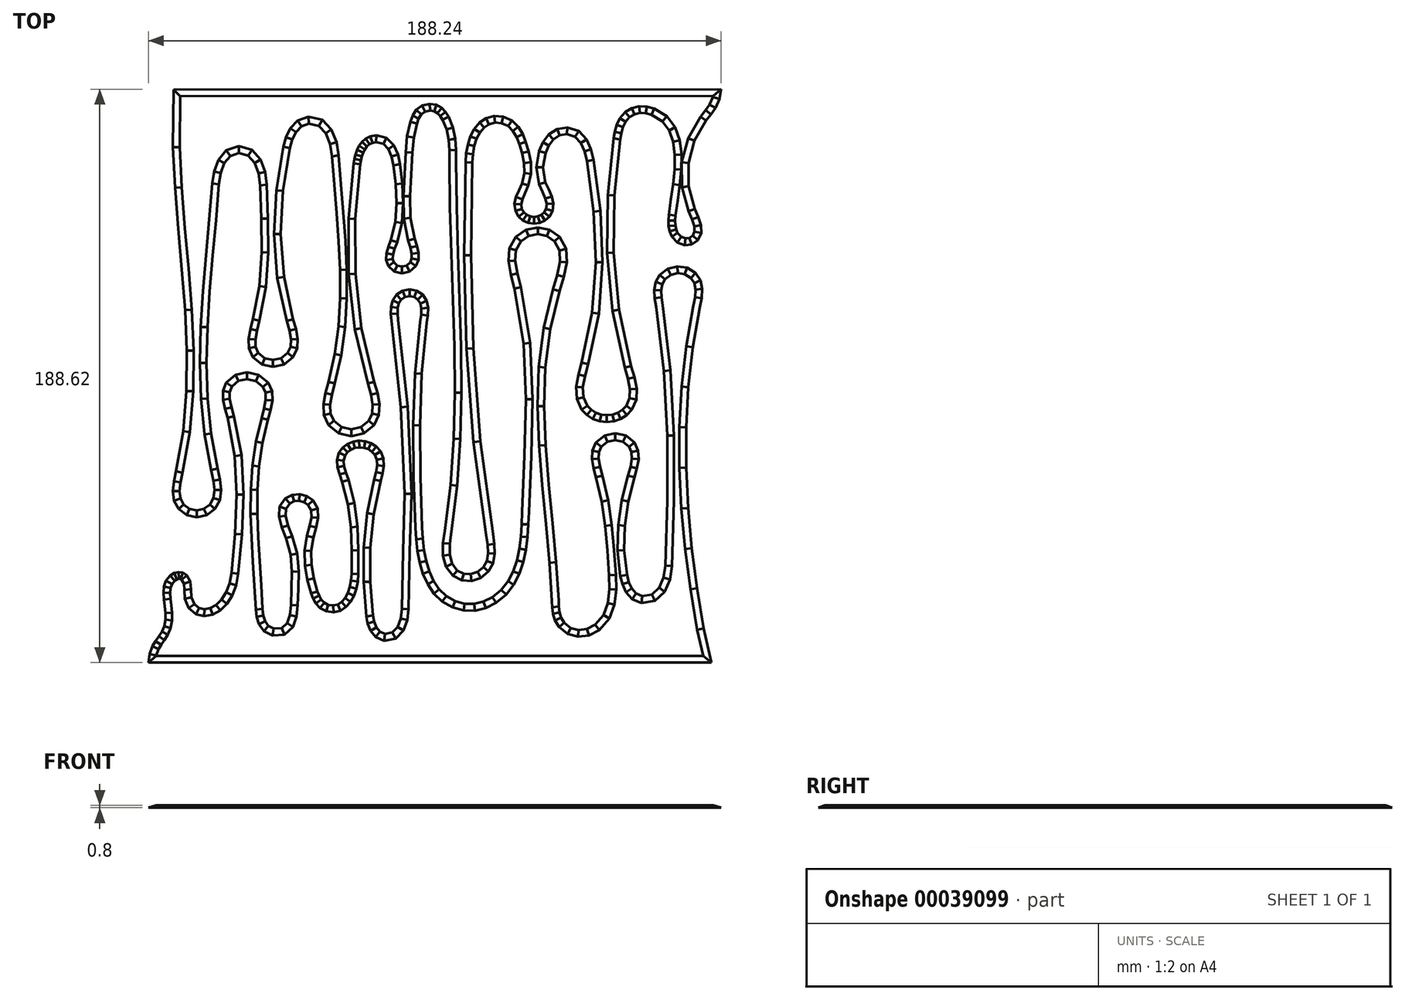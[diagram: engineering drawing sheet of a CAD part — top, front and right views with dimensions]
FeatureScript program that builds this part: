
annotation { "Feature Type Name" : "Feature", "Feature Type Description" : "" }
export const myFeature = defineFeature(function(context is Context, id is Id, definition is map)
    precondition{}
    {
        {
            var Q0;
            Q0=qCreatedBy(makeId("Top.planeOp"),FACE);
            var sketch = newSketch(context, id + "F0", { "sketchPlane" : qUnion([Q0])});
            skPoint(sketch, "E0.rect.middle", {"position": v(0, 0) * mm});
            skLineSegment(sketch, "E1", {"start": v(-85.88, 94.16) * mm, "end": v(-86.03, 75.24) * mm});
            skLineSegment(sketch, "E2", {"start": v(-86.03, 75.24) * mm, "end": v(-85.37, 61.84) * mm});
            skLineSegment(sketch, "E3", {"start": v(-85.37, 61.84) * mm, "end": v(-84.3, 48.43) * mm});
            skLineSegment(sketch, "E4", {"start": v(-84.3, 48.43) * mm, "end": v(-83.12, 35.03) * mm});
            skLineSegment(sketch, "E5", {"start": v(-83.12, 35.03) * mm, "end": v(-82.08, 21.66) * mm});
            skLineSegment(sketch, "E6", {"start": v(-82.08, 21.66) * mm, "end": v(-81.49, 8.31) * mm});
            skLineSegment(sketch, "E7", {"start": v(-81.49, 8.31) * mm, "end": v(-81.6, -4.99) * mm});
            skLineSegment(sketch, "E8", {"start": v(-81.6, -4.99) * mm, "end": v(-82.7, -18.23) * mm});
            skLineSegment(sketch, "E9", {"start": v(-82.7, -18.23) * mm, "end": v(-85.06, -31.41) * mm});
            skLineSegment(sketch, "E10", {"start": v(-85.06, -31.41) * mm, "end": v(-85.77, -34.7) * mm});
            skLineSegment(sketch, "E11", {"start": v(-85.77, -34.7) * mm, "end": v(-86.1, -37.97) * mm});
            skLineSegment(sketch, "E12", {"start": v(-86.1, -37.97) * mm, "end": v(-85.72, -41.07) * mm});
            skLineSegment(sketch, "E13", {"start": v(-85.72, -41.07) * mm, "end": v(-84.23, -43.82) * mm});
            skLineSegment(sketch, "E14", {"start": v(-84.23, -43.82) * mm, "end": v(-81.5, -45.83) * mm});
            skLineSegment(sketch, "E15", {"start": v(-81.5, -45.83) * mm, "end": v(-78.24, -46.5) * mm});
            skLineSegment(sketch, "E16", {"start": v(-78.24, -46.5) * mm, "end": v(-74.97, -45.83) * mm});
            skLineSegment(sketch, "E17", {"start": v(-74.97, -45.83) * mm, "end": v(-72.2, -43.82) * mm});
            skLineSegment(sketch, "E18", {"start": v(-72.2, -43.82) * mm, "end": v(-70.6, -40.9) * mm});
            skLineSegment(sketch, "E19", {"start": v(-70.6, -40.9) * mm, "end": v(-70.2, -37.59) * mm});
            skLineSegment(sketch, "E20", {"start": v(-70.2, -37.59) * mm, "end": v(-70.6, -34.08) * mm});
            skLineSegment(sketch, "E21", {"start": v(-70.6, -34.08) * mm, "end": v(-71.37, -30.56) * mm});
            skLineSegment(sketch, "E22", {"start": v(-71.37, -30.56) * mm, "end": v(-73.5, -19) * mm});
            skLineSegment(sketch, "E23", {"start": v(-73.5, -19) * mm, "end": v(-74.64, -7.39) * mm});
            skLineSegment(sketch, "E24", {"start": v(-74.64, -7.39) * mm, "end": v(-74.99, 4.28) * mm});
            skLineSegment(sketch, "E25", {"start": v(-74.99, 4.28) * mm, "end": v(-74.71, 16) * mm});
            skLineSegment(sketch, "E26", {"start": v(-74.71, 16) * mm, "end": v(-74, 27.74) * mm});
            skLineSegment(sketch, "E27", {"start": v(-74, 27.74) * mm, "end": v(-73, 39.5) * mm});
            skLineSegment(sketch, "E28", {"start": v(-73, 39.5) * mm, "end": v(-71.93, 51.26) * mm});
            skLineSegment(sketch, "E29", {"start": v(-71.93, 51.26) * mm, "end": v(-70.95, 63) * mm});
            skLineSegment(sketch, "E30", {"start": v(-70.95, 63) * mm, "end": v(-70.4, 66.7) * mm});
            skLineSegment(sketch, "E31", {"start": v(-70.4, 66.7) * mm, "end": v(-69.2, 69.99) * mm});
            skLineSegment(sketch, "E32", {"start": v(-69.2, 69.99) * mm, "end": v(-67.23, 72.36) * mm});
            skLineSegment(sketch, "E33", {"start": v(-67.23, 72.36) * mm, "end": v(-64.34, 73.32) * mm});
            skLineSegment(sketch, "E34", {"start": v(-64.34, 73.32) * mm, "end": v(-61.27, 72.45) * mm});
            skLineSegment(sketch, "E35", {"start": v(-61.27, 72.45) * mm, "end": v(-59.18, 70.02) * mm});
            skLineSegment(sketch, "E36", {"start": v(-59.18, 70.02) * mm, "end": v(-57.94, 66.58) * mm});
            skLineSegment(sketch, "E37", {"start": v(-57.94, 66.58) * mm, "end": v(-57.43, 62.68) * mm});
            skLineSegment(sketch, "E38", {"start": v(-57.43, 62.68) * mm, "end": v(-56.99, 51.73) * mm});
            skLineSegment(sketch, "E39", {"start": v(-56.99, 51.73) * mm, "end": v(-56.92, 40.64) * mm});
            skLineSegment(sketch, "E40", {"start": v(-56.92, 40.64) * mm, "end": v(-57.7, 29.56) * mm});
            skLineSegment(sketch, "E41", {"start": v(-57.7, 29.56) * mm, "end": v(-59.76, 18.63) * mm});
            skLineSegment(sketch, "E42", {"start": v(-59.76, 18.63) * mm, "end": v(-60.6, 15.4) * mm});
            skLineSegment(sketch, "E43", {"start": v(-60.6, 15.4) * mm, "end": v(-61.17, 12.17) * mm});
            skLineSegment(sketch, "E44", {"start": v(-61.17, 12.17) * mm, "end": v(-61.03, 9.06) * mm});
            skLineSegment(sketch, "E45", {"start": v(-61.03, 9.06) * mm, "end": v(-59.76, 6.2) * mm});
            skLineSegment(sketch, "E46", {"start": v(-59.76, 6.2) * mm, "end": v(-56.81, 3.76) * mm});
            skLineSegment(sketch, "E47", {"start": v(-56.81, 3.76) * mm, "end": v(-53.17, 2.94) * mm});
            skLineSegment(sketch, "E48", {"start": v(-53.17, 2.94) * mm, "end": v(-49.52, 3.76) * mm});
            skLineSegment(sketch, "E49", {"start": v(-49.52, 3.76) * mm, "end": v(-46.54, 6.2) * mm});
            skLineSegment(sketch, "E50", {"start": v(-46.54, 6.2) * mm, "end": v(-45.24, 9.06) * mm});
            skLineSegment(sketch, "E51", {"start": v(-45.24, 9.06) * mm, "end": v(-45.07, 12.17) * mm});
            skLineSegment(sketch, "E52", {"start": v(-45.07, 12.17) * mm, "end": v(-45.64, 15.4) * mm});
            skLineSegment(sketch, "E53", {"start": v(-45.64, 15.4) * mm, "end": v(-46.54, 18.63) * mm});
            skLineSegment(sketch, "E54", {"start": v(-46.54, 18.63) * mm, "end": v(-49.57, 32.54) * mm});
            skLineSegment(sketch, "E55", {"start": v(-49.57, 32.54) * mm, "end": v(-50.62, 46.66) * mm});
            skLineSegment(sketch, "E56", {"start": v(-50.62, 46.66) * mm, "end": v(-49.9, 60.84) * mm});
            skLineSegment(sketch, "E57", {"start": v(-49.9, 60.84) * mm, "end": v(-47.65, 74.93) * mm});
            skLineSegment(sketch, "E58", {"start": v(-47.65, 74.93) * mm, "end": v(-46.86, 77.72) * mm});
            skLineSegment(sketch, "E59", {"start": v(-46.86, 77.72) * mm, "end": v(-45.63, 80.22) * mm});
            skLineSegment(sketch, "E60", {"start": v(-45.63, 80.22) * mm, "end": v(-43.84, 82.08) * mm});
            skLineSegment(sketch, "E61", {"start": v(-43.84, 82.08) * mm, "end": v(-41.37, 82.94) * mm});
            skLineSegment(sketch, "E62", {"start": v(-41.37, 82.94) * mm, "end": v(-38.14, 82.23) * mm});
            skLineSegment(sketch, "E63", {"start": v(-38.14, 82.23) * mm, "end": v(-35.85, 79.82) * mm});
            skLineSegment(sketch, "E64", {"start": v(-35.85, 79.82) * mm, "end": v(-34.42, 76.3) * mm});
            skLineSegment(sketch, "E65", {"start": v(-34.42, 76.3) * mm, "end": v(-33.77, 72.24) * mm});
            skLineSegment(sketch, "E66", {"start": v(-33.77, 72.24) * mm, "end": v(-33.04, 62.9) * mm});
            skLineSegment(sketch, "E67", {"start": v(-33.04, 62.9) * mm, "end": v(-32.25, 53.55) * mm});
            skLineSegment(sketch, "E68", {"start": v(-32.25, 53.55) * mm, "end": v(-31.55, 44.2) * mm});
            skLineSegment(sketch, "E69", {"start": v(-31.55, 44.2) * mm, "end": v(-31.12, 34.86) * mm});
            skLineSegment(sketch, "E70", {"start": v(-31.12, 34.86) * mm, "end": v(-31.08, 25.56) * mm});
            skLineSegment(sketch, "E71", {"start": v(-31.08, 25.56) * mm, "end": v(-31.6, 16.31) * mm});
            skLineSegment(sketch, "E72", {"start": v(-31.6, 16.31) * mm, "end": v(-32.85, 7.14) * mm});
            skLineSegment(sketch, "E73", {"start": v(-32.85, 7.14) * mm, "end": v(-34.96, -1.95) * mm});
            skLineSegment(sketch, "E74", {"start": v(-34.96, -1.95) * mm, "end": v(-35.97, -5.64) * mm});
            skLineSegment(sketch, "E75", {"start": v(-35.97, -5.64) * mm, "end": v(-36.62, -9.34) * mm});
            skLineSegment(sketch, "E76", {"start": v(-36.62, -9.34) * mm, "end": v(-36.44, -12.9) * mm});
            skLineSegment(sketch, "E77", {"start": v(-36.44, -12.9) * mm, "end": v(-34.96, -16.15) * mm});
            skLineSegment(sketch, "E78", {"start": v(-34.96, -16.15) * mm, "end": v(-31.58, -18.92) * mm});
            skLineSegment(sketch, "E79", {"start": v(-31.58, -18.92) * mm, "end": v(-27.42, -19.84) * mm});
            skLineSegment(sketch, "E80", {"start": v(-27.42, -19.84) * mm, "end": v(-23.27, -18.92) * mm});
            skLineSegment(sketch, "E81", {"start": v(-23.27, -18.92) * mm, "end": v(-19.87, -16.15) * mm});
            skLineSegment(sketch, "E82", {"start": v(-19.87, -16.15) * mm, "end": v(-18.37, -12.9) * mm});
            skLineSegment(sketch, "E83", {"start": v(-18.37, -12.9) * mm, "end": v(-18.16, -9.34) * mm});
            skLineSegment(sketch, "E84", {"start": v(-18.16, -9.34) * mm, "end": v(-18.8, -5.64) * mm});
            skLineSegment(sketch, "E85", {"start": v(-18.8, -5.64) * mm, "end": v(-19.87, -1.95) * mm});
            skLineSegment(sketch, "E86", {"start": v(-19.87, -1.95) * mm, "end": v(-24.06, 15.66) * mm});
            skLineSegment(sketch, "E87", {"start": v(-24.06, 15.66) * mm, "end": v(-26.07, 33.57) * mm});
            skLineSegment(sketch, "E88", {"start": v(-26.07, 33.57) * mm, "end": v(-26.14, 51.63) * mm});
            skLineSegment(sketch, "E89", {"start": v(-26.14, 51.63) * mm, "end": v(-24.51, 69.66) * mm});
            skLineSegment(sketch, "E90", {"start": v(-24.51, 69.66) * mm, "end": v(-24.3, 70.97) * mm});
            skLineSegment(sketch, "E91", {"start": v(-24.3, 70.97) * mm, "end": v(-23.98, 72.24) * mm});
            skLineSegment(sketch, "E92", {"start": v(-23.98, 72.24) * mm, "end": v(-23.54, 73.44) * mm});
            skLineSegment(sketch, "E93", {"start": v(-23.54, 73.44) * mm, "end": v(-22.99, 74.52) * mm});
            skLineSegment(sketch, "E94", {"start": v(-22.99, 74.52) * mm, "end": v(-22.3, 75.46) * mm});
            skLineSegment(sketch, "E95", {"start": v(-22.3, 75.46) * mm, "end": v(-21.45, 76.2) * mm});
            skLineSegment(sketch, "E96", {"start": v(-21.45, 76.2) * mm, "end": v(-20.45, 76.68) * mm});
            skLineSegment(sketch, "E97", {"start": v(-20.45, 76.68) * mm, "end": v(-19.27, 76.9) * mm});
            skLineSegment(sketch, "E98", {"start": v(-19.27, 76.9) * mm, "end": v(-16.93, 76.32) * mm});
            skLineSegment(sketch, "E99", {"start": v(-16.93, 76.32) * mm, "end": v(-15.25, 74.6) * mm});
            skLineSegment(sketch, "E100", {"start": v(-15.25, 74.6) * mm, "end": v(-14.16, 72.14) * mm});
            skLineSegment(sketch, "E101", {"start": v(-14.16, 72.14) * mm, "end": v(-13.57, 69.31) * mm});
            skLineSegment(sketch, "E102", {"start": v(-13.57, 69.31) * mm, "end": v(-12.87, 63.07) * mm});
            skLineSegment(sketch, "E103", {"start": v(-12.87, 63.07) * mm, "end": v(-12.55, 56.82) * mm});
            skLineSegment(sketch, "E104", {"start": v(-12.55, 56.82) * mm, "end": v(-12.96, 50.66) * mm});
            skLineSegment(sketch, "E105", {"start": v(-12.96, 50.66) * mm, "end": v(-14.46, 44.65) * mm});
            skLineSegment(sketch, "E106", {"start": v(-14.46, 44.65) * mm, "end": v(-15.27, 42.47) * mm});
            skLineSegment(sketch, "E107", {"start": v(-15.27, 42.47) * mm, "end": v(-15.9, 40.27) * mm});
            skLineSegment(sketch, "E108", {"start": v(-15.9, 40.27) * mm, "end": v(-16.01, 38.12) * mm});
            skLineSegment(sketch, "E109", {"start": v(-16.01, 38.12) * mm, "end": v(-15.3, 36.09) * mm});
            skLineSegment(sketch, "E110", {"start": v(-15.3, 36.09) * mm, "end": v(-13.3, 34.29) * mm});
            skLineSegment(sketch, "E111", {"start": v(-13.3, 34.29) * mm, "end": v(-10.78, 33.68) * mm});
            skLineSegment(sketch, "E112", {"start": v(-10.78, 33.68) * mm, "end": v(-8.23, 34.29) * mm});
            skLineSegment(sketch, "E113", {"start": v(-8.23, 34.29) * mm, "end": v(-6.18, 36.09) * mm});
            skLineSegment(sketch, "E114", {"start": v(-6.18, 36.09) * mm, "end": v(-5.35, 38.2) * mm});
            skLineSegment(sketch, "E115", {"start": v(-5.35, 38.2) * mm, "end": v(-5.36, 40.44) * mm});
            skLineSegment(sketch, "E116", {"start": v(-5.36, 40.44) * mm, "end": v(-5.88, 42.76) * mm});
            skLineSegment(sketch, "E117", {"start": v(-5.88, 42.76) * mm, "end": v(-6.6, 45.08) * mm});
            skLineSegment(sketch, "E118", {"start": v(-6.6, 45.08) * mm, "end": v(-7.94, 52.04) * mm});
            skLineSegment(sketch, "E119", {"start": v(-7.94, 52.04) * mm, "end": v(-8.13, 59.11) * mm});
            skLineSegment(sketch, "E120", {"start": v(-8.13, 59.11) * mm, "end": v(-7.74, 66.26) * mm});
            skLineSegment(sketch, "E121", {"start": v(-7.74, 66.26) * mm, "end": v(-7.38, 73.42) * mm});
            skLineSegment(sketch, "E122", {"start": v(-7.38, 73.42) * mm, "end": v(-6.9, 78.46) * mm});
            skLineSegment(sketch, "E123", {"start": v(-6.9, 78.46) * mm, "end": v(-5.89, 82.97) * mm});
            skLineSegment(sketch, "E124", {"start": v(-5.89, 82.97) * mm, "end": v(-5.28, 84.62) * mm});
            skLineSegment(sketch, "E125", {"start": v(-5.28, 84.62) * mm, "end": v(-4.41, 85.98) * mm});
            skLineSegment(sketch, "E126", {"start": v(-4.41, 85.98) * mm, "end": v(-3.2, 86.92) * mm});
            skLineSegment(sketch, "E127", {"start": v(-3.2, 86.92) * mm, "end": v(-1.55, 87.29) * mm});
            skLineSegment(sketch, "E128", {"start": v(-1.55, 87.29) * mm, "end": v(-0.17, 87.07) * mm});
            skLineSegment(sketch, "E129", {"start": v(-0.17, 87.07) * mm, "end": v(0.94, 86.43) * mm});
            skLineSegment(sketch, "E130", {"start": v(0.94, 86.43) * mm, "end": v(1.85, 85.47) * mm});
            skLineSegment(sketch, "E131", {"start": v(1.85, 85.47) * mm, "end": v(2.61, 84.27) * mm});
            skLineSegment(sketch, "E132", {"start": v(2.61, 84.27) * mm, "end": v(3.93, 81.06) * mm});
            skLineSegment(sketch, "E133", {"start": v(3.93, 81.06) * mm, "end": v(4.6, 77.68) * mm});
            skLineSegment(sketch, "E134", {"start": v(4.6, 77.68) * mm, "end": v(4.83, 74.2) * mm});
            skLineSegment(sketch, "E135", {"start": v(4.83, 74.2) * mm, "end": v(4.85, 70.7) * mm});
            skLineSegment(sketch, "E136", {"start": v(4.85, 70.7) * mm, "end": v(5, 55.46) * mm});
            skLineSegment(sketch, "E137", {"start": v(5, 55.46) * mm, "end": v(5.45, 40.2) * mm});
            skLineSegment(sketch, "E138", {"start": v(5.45, 40.2) * mm, "end": v(6, 24.96) * mm});
            skLineSegment(sketch, "E139", {"start": v(6, 24.96) * mm, "end": v(6.46, 9.72) * mm});
            skLineSegment(sketch, "E140", {"start": v(6.46, 9.72) * mm, "end": v(6.61, -5.5) * mm});
            skLineSegment(sketch, "E141", {"start": v(6.61, -5.5) * mm, "end": v(6.27, -20.7) * mm});
            skLineSegment(sketch, "E142", {"start": v(6.27, -20.7) * mm, "end": v(5.22, -35.87) * mm});
            skLineSegment(sketch, "E143", {"start": v(5.22, -35.87) * mm, "end": v(3.27, -51) * mm});
            skLineSegment(sketch, "E144", {"start": v(3.27, -51) * mm, "end": v(2.74, -55.1) * mm});
            skLineSegment(sketch, "E145", {"start": v(2.74, -55.1) * mm, "end": v(2.74, -59.14) * mm});
            skLineSegment(sketch, "E146", {"start": v(2.74, -59.14) * mm, "end": v(3.68, -62.8) * mm});
            skLineSegment(sketch, "E147", {"start": v(3.68, -62.8) * mm, "end": v(5.98, -65.76) * mm});
            skLineSegment(sketch, "E148", {"start": v(5.98, -65.76) * mm, "end": v(8.89, -67.24) * mm});
            skLineSegment(sketch, "E149", {"start": v(8.89, -67.24) * mm, "end": v(12.09, -67.45) * mm});
            skLineSegment(sketch, "E150", {"start": v(12.09, -67.45) * mm, "end": v(15.17, -66.47) * mm});
            skLineSegment(sketch, "E151", {"start": v(15.17, -66.47) * mm, "end": v(17.73, -64.36) * mm});
            skLineSegment(sketch, "E152", {"start": v(17.73, -64.36) * mm, "end": v(19.21, -61.61) * mm});
            skLineSegment(sketch, "E153", {"start": v(19.21, -61.61) * mm, "end": v(19.74, -58.55) * mm});
            skLineSegment(sketch, "E154", {"start": v(19.74, -58.55) * mm, "end": v(19.61, -55.32) * mm});
            skLineSegment(sketch, "E155", {"start": v(19.61, -55.32) * mm, "end": v(19.13, -52.07) * mm});
            skLineSegment(sketch, "E156", {"start": v(19.13, -52.07) * mm, "end": v(14.94, -21.59) * mm});
            skLineSegment(sketch, "E157", {"start": v(14.94, -21.59) * mm, "end": v(12.66, 9.04) * mm});
            skLineSegment(sketch, "E158", {"start": v(12.66, 9.04) * mm, "end": v(11.9, 39.69) * mm});
            skLineSegment(sketch, "E159", {"start": v(11.9, 39.69) * mm, "end": v(12.31, 70.2) * mm});
            skLineSegment(sketch, "E160", {"start": v(12.31, 70.2) * mm, "end": v(12.53, 72.97) * mm});
            skLineSegment(sketch, "E161", {"start": v(12.53, 72.97) * mm, "end": v(13.02, 75.6) * mm});
            skLineSegment(sketch, "E162", {"start": v(13.02, 75.6) * mm, "end": v(13.8, 77.99) * mm});
            skLineSegment(sketch, "E163", {"start": v(13.8, 77.99) * mm, "end": v(14.86, 80.04) * mm});
            skLineSegment(sketch, "E164", {"start": v(14.86, 80.04) * mm, "end": v(16.2, 81.67) * mm});
            skLineSegment(sketch, "E165", {"start": v(16.2, 81.67) * mm, "end": v(17.84, 82.79) * mm});
            skLineSegment(sketch, "E166", {"start": v(17.84, 82.79) * mm, "end": v(19.78, 83.3) * mm});
            skLineSegment(sketch, "E167", {"start": v(19.78, 83.3) * mm, "end": v(22, 83.12) * mm});
            skLineSegment(sketch, "E168", {"start": v(22, 83.12) * mm, "end": v(24.12, 82.17) * mm});
            skLineSegment(sketch, "E169", {"start": v(24.12, 82.17) * mm, "end": v(25.74, 80.57) * mm});
            skLineSegment(sketch, "E170", {"start": v(25.74, 80.57) * mm, "end": v(26.95, 78.54) * mm});
            skLineSegment(sketch, "E171", {"start": v(26.95, 78.54) * mm, "end": v(27.83, 76.3) * mm});
            skLineSegment(sketch, "E172", {"start": v(27.83, 76.3) * mm, "end": v(28.74, 73.29) * mm});
            skLineSegment(sketch, "E173", {"start": v(28.74, 73.29) * mm, "end": v(29.4, 70.05) * mm});
            skLineSegment(sketch, "E174", {"start": v(29.4, 70.05) * mm, "end": v(29.48, 66.7) * mm});
            skLineSegment(sketch, "E175", {"start": v(29.48, 66.7) * mm, "end": v(28.71, 63.34) * mm});
            skLineSegment(sketch, "E176", {"start": v(28.71, 63.34) * mm, "end": v(27.7, 61.07) * mm});
            skLineSegment(sketch, "E177", {"start": v(27.7, 61.07) * mm, "end": v(26.75, 58.81) * mm});
            skLineSegment(sketch, "E178", {"start": v(26.75, 58.81) * mm, "end": v(26.22, 56.55) * mm});
            skLineSegment(sketch, "E179", {"start": v(26.22, 56.55) * mm, "end": v(26.52, 54.25) * mm});
            skLineSegment(sketch, "E180", {"start": v(26.52, 54.25) * mm, "end": v(27.55, 52.42) * mm});
            skLineSegment(sketch, "E181", {"start": v(27.55, 52.42) * mm, "end": v(29, 51.11) * mm});
            skLineSegment(sketch, "E182", {"start": v(29, 51.11) * mm, "end": v(30.73, 50.33) * mm});
            skLineSegment(sketch, "E183", {"start": v(30.73, 50.33) * mm, "end": v(32.62, 50.06) * mm});
            skLineSegment(sketch, "E184", {"start": v(32.62, 50.06) * mm, "end": v(34.5, 50.32) * mm});
            skLineSegment(sketch, "E185", {"start": v(34.5, 50.32) * mm, "end": v(36.24, 51.1) * mm});
            skLineSegment(sketch, "E186", {"start": v(36.24, 51.1) * mm, "end": v(37.7, 52.42) * mm});
            skLineSegment(sketch, "E187", {"start": v(37.7, 52.42) * mm, "end": v(38.73, 54.25) * mm});
            skLineSegment(sketch, "E188", {"start": v(38.73, 54.25) * mm, "end": v(39.04, 56.65) * mm});
            skLineSegment(sketch, "E189", {"start": v(39.04, 56.65) * mm, "end": v(38.47, 59) * mm});
            skLineSegment(sketch, "E190", {"start": v(38.47, 59) * mm, "end": v(37.44, 61.35) * mm});
            skLineSegment(sketch, "E191", {"start": v(37.44, 61.35) * mm, "end": v(36.38, 63.72) * mm});
            skLineSegment(sketch, "E192", {"start": v(36.38, 63.72) * mm, "end": v(35.6, 68.65) * mm});
            skLineSegment(sketch, "E193", {"start": v(35.6, 68.65) * mm, "end": v(36.44, 73.33) * mm});
            skLineSegment(sketch, "E194", {"start": v(36.44, 73.33) * mm, "end": v(37.49, 75.76) * mm});
            skLineSegment(sketch, "E195", {"start": v(37.49, 75.76) * mm, "end": v(39.04, 77.78) * mm});
            skLineSegment(sketch, "E196", {"start": v(39.04, 77.78) * mm, "end": v(41.04, 79.12) * mm});
            skLineSegment(sketch, "E197", {"start": v(41.04, 79.12) * mm, "end": v(43.45, 79.51) * mm});
            skLineSegment(sketch, "E198", {"start": v(43.45, 79.51) * mm, "end": v(46.11, 78.62) * mm});
            skLineSegment(sketch, "E199", {"start": v(46.11, 78.62) * mm, "end": v(48.02, 76.6) * mm});
            skLineSegment(sketch, "E200", {"start": v(48.02, 76.6) * mm, "end": v(49.3, 73.82) * mm});
            skLineSegment(sketch, "E201", {"start": v(49.3, 73.82) * mm, "end": v(50.05, 70.68) * mm});
            skLineSegment(sketch, "E202", {"start": v(50.05, 70.68) * mm, "end": v(52.24, 54.05) * mm});
            skLineSegment(sketch, "E203", {"start": v(52.24, 54.05) * mm, "end": v(52.94, 37.37) * mm});
            skLineSegment(sketch, "E204", {"start": v(52.94, 37.37) * mm, "end": v(51.75, 20.79) * mm});
            skLineSegment(sketch, "E205", {"start": v(51.75, 20.79) * mm, "end": v(48.32, 4.42) * mm});
            skLineSegment(sketch, "E206", {"start": v(48.32, 4.42) * mm, "end": v(47.2, 0.4) * mm});
            skLineSegment(sketch, "E207", {"start": v(47.2, 0.4) * mm, "end": v(46.5, -3.65) * mm});
            skLineSegment(sketch, "E208", {"start": v(46.5, -3.65) * mm, "end": v(46.71, -7.53) * mm});
            skLineSegment(sketch, "E209", {"start": v(46.71, -7.53) * mm, "end": v(48.32, -11.1) * mm});
            skLineSegment(sketch, "E210", {"start": v(48.32, -11.1) * mm, "end": v(50, -12.87) * mm});
            skLineSegment(sketch, "E211", {"start": v(50, -12.87) * mm, "end": v(52.01, -14.14) * mm});
            skLineSegment(sketch, "E212", {"start": v(52.01, -14.14) * mm, "end": v(54.24, -14.91) * mm});
            skLineSegment(sketch, "E213", {"start": v(54.24, -14.91) * mm, "end": v(56.57, -15.17) * mm});
            skLineSegment(sketch, "E214", {"start": v(56.57, -15.17) * mm, "end": v(58.9, -14.92) * mm});
            skLineSegment(sketch, "E215", {"start": v(58.9, -14.92) * mm, "end": v(61.13, -14.16) * mm});
            skLineSegment(sketch, "E216", {"start": v(61.13, -14.16) * mm, "end": v(63.14, -12.89) * mm});
            skLineSegment(sketch, "E217", {"start": v(63.14, -12.89) * mm, "end": v(64.83, -11.1) * mm});
            skLineSegment(sketch, "E218", {"start": v(64.83, -11.1) * mm, "end": v(66.26, -7.8) * mm});
            skLineSegment(sketch, "E219", {"start": v(66.26, -7.8) * mm, "end": v(66.37, -4.23) * mm});
            skLineSegment(sketch, "E220", {"start": v(66.37, -4.23) * mm, "end": v(65.65, -0.49) * mm});
            skLineSegment(sketch, "E221", {"start": v(65.65, -0.49) * mm, "end": v(64.59, 3.27) * mm});
            skLineSegment(sketch, "E222", {"start": v(64.59, 3.27) * mm, "end": v(60.57, 21.74) * mm});
            skLineSegment(sketch, "E223", {"start": v(60.57, 21.74) * mm, "end": v(58.84, 40.52) * mm});
            skLineSegment(sketch, "E224", {"start": v(58.84, 40.52) * mm, "end": v(59.1, 59.31) * mm});
            skLineSegment(sketch, "E225", {"start": v(59.1, 59.31) * mm, "end": v(61, 77.8) * mm});
            skLineSegment(sketch, "E226", {"start": v(61, 77.8) * mm, "end": v(61.35, 79.83) * mm});
            skLineSegment(sketch, "E227", {"start": v(61.35, 79.83) * mm, "end": v(61.89, 81.8) * mm});
            skLineSegment(sketch, "E228", {"start": v(61.89, 81.8) * mm, "end": v(62.75, 83.6) * mm});
            skLineSegment(sketch, "E229", {"start": v(62.75, 83.6) * mm, "end": v(64.04, 85.09) * mm});
            skLineSegment(sketch, "E230", {"start": v(64.04, 85.09) * mm, "end": v(65.67, 86.06) * mm});
            skLineSegment(sketch, "E231", {"start": v(65.67, 86.06) * mm, "end": v(67.48, 86.5) * mm});
            skLineSegment(sketch, "E232", {"start": v(67.48, 86.5) * mm, "end": v(69.38, 86.44) * mm});
            skLineSegment(sketch, "E233", {"start": v(69.38, 86.44) * mm, "end": v(71.25, 85.93) * mm});
            skLineSegment(sketch, "E234", {"start": v(71.25, 85.93) * mm, "end": v(74.78, 83.76) * mm});
            skLineSegment(sketch, "E235", {"start": v(74.78, 83.76) * mm, "end": v(77.1, 80.73) * mm});
            skLineSegment(sketch, "E236", {"start": v(77.1, 80.73) * mm, "end": v(78.42, 77) * mm});
            skLineSegment(sketch, "E237", {"start": v(78.42, 77) * mm, "end": v(78.93, 72.71) * mm});
            skLineSegment(sketch, "E238", {"start": v(78.93, 72.71) * mm, "end": v(78.84, 68.02) * mm});
            skLineSegment(sketch, "E239", {"start": v(78.84, 68.02) * mm, "end": v(78.35, 63.08) * mm});
            skLineSegment(sketch, "E240", {"start": v(78.35, 63.08) * mm, "end": v(77.67, 58.03) * mm});
            skLineSegment(sketch, "E241", {"start": v(77.67, 58.03) * mm, "end": v(77, 53.04) * mm});
            skLineSegment(sketch, "E242", {"start": v(77, 53.04) * mm, "end": v(76.84, 51.16) * mm});
            skLineSegment(sketch, "E243", {"start": v(76.84, 51.16) * mm, "end": v(76.88, 49.3) * mm});
            skLineSegment(sketch, "E244", {"start": v(76.88, 49.3) * mm, "end": v(77.22, 47.5) * mm});
            skLineSegment(sketch, "E245", {"start": v(77.22, 47.5) * mm, "end": v(77.97, 45.81) * mm});
            skLineSegment(sketch, "E246", {"start": v(77.97, 45.81) * mm, "end": v(79.83, 43.88) * mm});
            skLineSegment(sketch, "E247", {"start": v(79.83, 43.88) * mm, "end": v(82.15, 42.99) * mm});
            skLineSegment(sketch, "E248", {"start": v(82.15, 42.99) * mm, "end": v(84.52, 43.21) * mm});
            skLineSegment(sketch, "E249", {"start": v(84.52, 43.21) * mm, "end": v(86.55, 44.64) * mm});
            skLineSegment(sketch, "E250", {"start": v(86.55, 44.64) * mm, "end": v(87.63, 46.98) * mm});
            skLineSegment(sketch, "E251", {"start": v(87.63, 46.98) * mm, "end": v(87.51, 49.54) * mm});
            skLineSegment(sketch, "E252", {"start": v(87.51, 49.54) * mm, "end": v(86.65, 52.21) * mm});
            skLineSegment(sketch, "E253", {"start": v(86.65, 52.21) * mm, "end": v(85.5, 54.9) * mm});
            skLineSegment(sketch, "E254", {"start": v(85.5, 54.9) * mm, "end": v(83.43, 62.36) * mm});
            skLineSegment(sketch, "E255", {"start": v(83.43, 62.36) * mm, "end": v(83.4, 69.97) * mm});
            skLineSegment(sketch, "E256", {"start": v(83.4, 69.97) * mm, "end": v(85.34, 77.33) * mm});
            skLineSegment(sketch, "E257", {"start": v(85.34, 77.33) * mm, "end": v(89.17, 84.03) * mm});
            skLineSegment(sketch, "E258", {"start": v(89.17, 84.03) * mm, "end": v(90.8, 86.06) * mm});
            skLineSegment(sketch, "E259", {"start": v(90.8, 86.06) * mm, "end": v(92.3, 88.17) * mm});
            skLineSegment(sketch, "E260", {"start": v(92.3, 88.17) * mm, "end": v(93.6, 91.12) * mm});
            skLineSegment(sketch, "E261", {"start": v(93.6, 91.12) * mm, "end": v(94.12, 94.31) * mm});
            skLineSegment(sketch, "E262", {"start": v(94.12, 94.31) * mm, "end": v(-85.88, 94.16) * mm});
            skLineSegment(sketch, "E263", {"start": v(90.97, -94.31) * mm, "end": v(88.4, -83.08) * mm});
            skLineSegment(sketch, "E264", {"start": v(88.4, -83.08) * mm, "end": v(86.2, -69.9) * mm});
            skLineSegment(sketch, "E265", {"start": v(86.2, -69.9) * mm, "end": v(84.48, -56.7) * mm});
            skLineSegment(sketch, "E266", {"start": v(84.48, -56.7) * mm, "end": v(83.26, -43.45) * mm});
            skLineSegment(sketch, "E267", {"start": v(83.26, -43.45) * mm, "end": v(82.63, -30.2) * mm});
            skLineSegment(sketch, "E268", {"start": v(82.63, -30.2) * mm, "end": v(82.64, -16.95) * mm});
            skLineSegment(sketch, "E269", {"start": v(82.64, -16.95) * mm, "end": v(83.36, -3.74) * mm});
            skLineSegment(sketch, "E270", {"start": v(83.36, -3.74) * mm, "end": v(84.85, 9.44) * mm});
            skLineSegment(sketch, "E271", {"start": v(84.85, 9.44) * mm, "end": v(87.18, 22.54) * mm});
            skLineSegment(sketch, "E272", {"start": v(87.18, 22.54) * mm, "end": v(87.74, 25.57) * mm});
            skLineSegment(sketch, "E273", {"start": v(87.74, 25.57) * mm, "end": v(87.92, 28.57) * mm});
            skLineSegment(sketch, "E274", {"start": v(87.92, 28.57) * mm, "end": v(87.39, 31.38) * mm});
            skLineSegment(sketch, "E275", {"start": v(87.39, 31.38) * mm, "end": v(85.8, 33.83) * mm});
            skLineSegment(sketch, "E276", {"start": v(85.8, 33.83) * mm, "end": v(83, 35.59) * mm});
            skLineSegment(sketch, "E277", {"start": v(83, 35.59) * mm, "end": v(79.78, 36.05) * mm});
            skLineSegment(sketch, "E278", {"start": v(79.78, 36.05) * mm, "end": v(76.61, 35.27) * mm});
            skLineSegment(sketch, "E279", {"start": v(76.61, 35.27) * mm, "end": v(73.98, 33.26) * mm});
            skLineSegment(sketch, "E280", {"start": v(73.98, 33.26) * mm, "end": v(72.67, 30.91) * mm});
            skLineSegment(sketch, "E281", {"start": v(72.67, 30.91) * mm, "end": v(72.2, 28.3) * mm});
            skLineSegment(sketch, "E282", {"start": v(72.2, 28.3) * mm, "end": v(72.32, 25.56) * mm});
            skLineSegment(sketch, "E283", {"start": v(72.32, 25.56) * mm, "end": v(72.73, 22.8) * mm});
            skLineSegment(sketch, "E284", {"start": v(72.73, 22.8) * mm, "end": v(75.34, 1.61) * mm});
            skLineSegment(sketch, "E285", {"start": v(75.34, 1.61) * mm, "end": v(76.41, -19.7) * mm});
            skLineSegment(sketch, "E286", {"start": v(76.41, -19.7) * mm, "end": v(76.42, -41.05) * mm});
            skLineSegment(sketch, "E287", {"start": v(76.42, -41.05) * mm, "end": v(75.85, -62.42) * mm});
            skLineSegment(sketch, "E288", {"start": v(75.85, -62.42) * mm, "end": v(75.25, -66.38) * mm});
            skLineSegment(sketch, "E289", {"start": v(75.25, -66.38) * mm, "end": v(73.75, -69.73) * mm});
            skLineSegment(sketch, "E290", {"start": v(73.75, -69.73) * mm, "end": v(71.41, -71.93) * mm});
            skLineSegment(sketch, "E291", {"start": v(71.41, -71.93) * mm, "end": v(68.27, -72.43) * mm});
            skLineSegment(sketch, "E292", {"start": v(68.27, -72.43) * mm, "end": v(66.23, -71.6) * mm});
            skLineSegment(sketch, "E293", {"start": v(66.23, -71.6) * mm, "end": v(64.77, -69.97) * mm});
            skLineSegment(sketch, "E294", {"start": v(64.77, -69.97) * mm, "end": v(63.8, -67.85) * mm});
            skLineSegment(sketch, "E295", {"start": v(63.8, -67.85) * mm, "end": v(63.2, -65.5) * mm});
            skLineSegment(sketch, "E296", {"start": v(63.2, -65.5) * mm, "end": v(62.3, -57.42) * mm});
            skLineSegment(sketch, "E297", {"start": v(62.3, -57.42) * mm, "end": v(62.5, -49.32) * mm});
            skLineSegment(sketch, "E298", {"start": v(62.5, -49.32) * mm, "end": v(63.66, -41.3) * mm});
            skLineSegment(sketch, "E299", {"start": v(63.66, -41.3) * mm, "end": v(65.65, -33.38) * mm});
            skLineSegment(sketch, "E300", {"start": v(65.65, -33.38) * mm, "end": v(66.5, -30.41) * mm});
            skLineSegment(sketch, "E301", {"start": v(66.5, -30.41) * mm, "end": v(67.03, -27.43) * mm});
            skLineSegment(sketch, "E302", {"start": v(67.03, -27.43) * mm, "end": v(66.87, -24.56) * mm});
            skLineSegment(sketch, "E303", {"start": v(66.87, -24.56) * mm, "end": v(65.65, -21.93) * mm});
            skLineSegment(sketch, "E304", {"start": v(65.65, -21.93) * mm, "end": v(62.82, -19.67) * mm});
            skLineSegment(sketch, "E305", {"start": v(62.82, -19.67) * mm, "end": v(59.34, -18.92) * mm});
            skLineSegment(sketch, "E306", {"start": v(59.34, -18.92) * mm, "end": v(55.86, -19.67) * mm});
            skLineSegment(sketch, "E307", {"start": v(55.86, -19.67) * mm, "end": v(53.02, -21.93) * mm});
            skLineSegment(sketch, "E308", {"start": v(53.02, -21.93) * mm, "end": v(51.81, -24.55) * mm});
            skLineSegment(sketch, "E309", {"start": v(51.81, -24.55) * mm, "end": v(51.67, -27.42) * mm});
            skLineSegment(sketch, "E310", {"start": v(51.67, -27.42) * mm, "end": v(52.2, -30.4) * mm});
            skLineSegment(sketch, "E311", {"start": v(52.2, -30.4) * mm, "end": v(53.02, -33.38) * mm});
            skLineSegment(sketch, "E312", {"start": v(53.02, -33.38) * mm, "end": v(54.83, -41.33) * mm});
            skLineSegment(sketch, "E313", {"start": v(54.83, -41.33) * mm, "end": v(55.99, -49.38) * mm});
            skLineSegment(sketch, "E314", {"start": v(55.99, -49.38) * mm, "end": v(56.75, -57.5) * mm});
            skLineSegment(sketch, "E315", {"start": v(56.75, -57.5) * mm, "end": v(57.34, -65.64) * mm});
            skLineSegment(sketch, "E316", {"start": v(57.34, -65.64) * mm, "end": v(57.47, -70.24) * mm});
            skLineSegment(sketch, "E317", {"start": v(57.47, -70.24) * mm, "end": v(56.95, -74.71) * mm});
            skLineSegment(sketch, "E318", {"start": v(56.95, -74.71) * mm, "end": v(55.47, -78.71) * mm});
            skLineSegment(sketch, "E319", {"start": v(55.47, -78.71) * mm, "end": v(52.68, -81.91) * mm});
            skLineSegment(sketch, "E320", {"start": v(52.68, -81.91) * mm, "end": v(50.08, -83.26) * mm});
            skLineSegment(sketch, "E321", {"start": v(50.08, -83.26) * mm, "end": v(47.32, -83.63) * mm});
            skLineSegment(sketch, "E322", {"start": v(47.32, -83.63) * mm, "end": v(44.7, -82.96) * mm});
            skLineSegment(sketch, "E323", {"start": v(44.7, -82.96) * mm, "end": v(42.54, -81.22) * mm});
            skLineSegment(sketch, "E324", {"start": v(42.54, -81.22) * mm, "end": v(41.6, -79.61) * mm});
            skLineSegment(sketch, "E325", {"start": v(41.6, -79.61) * mm, "end": v(41.07, -77.82) * mm});
            skLineSegment(sketch, "E326", {"start": v(41.07, -77.82) * mm, "end": v(40.82, -75.92) * mm});
            skLineSegment(sketch, "E327", {"start": v(40.82, -75.92) * mm, "end": v(40.73, -73.99) * mm});
            skLineSegment(sketch, "E328", {"start": v(40.73, -73.99) * mm, "end": v(39.95, -61.35) * mm});
            skLineSegment(sketch, "E329", {"start": v(39.95, -61.35) * mm, "end": v(38.78, -48.58) * mm});
            skLineSegment(sketch, "E330", {"start": v(38.78, -48.58) * mm, "end": v(37.53, -35.74) * mm});
            skLineSegment(sketch, "E331", {"start": v(37.53, -35.74) * mm, "end": v(36.5, -22.87) * mm});
            skLineSegment(sketch, "E332", {"start": v(36.5, -22.87) * mm, "end": v(36.02, -10.02) * mm});
            skLineSegment(sketch, "E333", {"start": v(36.02, -10.02) * mm, "end": v(36.4, 2.75) * mm});
            skLineSegment(sketch, "E334", {"start": v(36.4, 2.75) * mm, "end": v(37.95, 15.4) * mm});
            skLineSegment(sketch, "E335", {"start": v(37.95, 15.4) * mm, "end": v(40.99, 27.88) * mm});
            skLineSegment(sketch, "E336", {"start": v(40.99, 27.88) * mm, "end": v(42.45, 32.62) * mm});
            skLineSegment(sketch, "E337", {"start": v(42.45, 32.62) * mm, "end": v(43.42, 37.35) * mm});
            skLineSegment(sketch, "E338", {"start": v(43.42, 37.35) * mm, "end": v(43.2, 41.82) * mm});
            skLineSegment(sketch, "E339", {"start": v(43.2, 41.82) * mm, "end": v(41.08, 45.78) * mm});
            skLineSegment(sketch, "E340", {"start": v(41.08, 45.78) * mm, "end": v(37.76, 48.1) * mm});
            skLineSegment(sketch, "E341", {"start": v(37.76, 48.1) * mm, "end": v(33.88, 48.87) * mm});
            skLineSegment(sketch, "E342", {"start": v(33.88, 48.87) * mm, "end": v(29.99, 48.1) * mm});
            skLineSegment(sketch, "E343", {"start": v(29.99, 48.1) * mm, "end": v(26.67, 45.78) * mm});
            skLineSegment(sketch, "E344", {"start": v(26.67, 45.78) * mm, "end": v(24.59, 42.02) * mm});
            skLineSegment(sketch, "E345", {"start": v(24.59, 42.02) * mm, "end": v(24.26, 37.76) * mm});
            skLineSegment(sketch, "E346", {"start": v(24.26, 37.76) * mm, "end": v(25, 33.25) * mm});
            skLineSegment(sketch, "E347", {"start": v(25, 33.25) * mm, "end": v(26.16, 28.7) * mm});
            skLineSegment(sketch, "E348", {"start": v(26.16, 28.7) * mm, "end": v(29.21, 10.62) * mm});
            skLineSegment(sketch, "E349", {"start": v(29.21, 10.62) * mm, "end": v(30, -7.74) * mm});
            skLineSegment(sketch, "E350", {"start": v(30, -7.74) * mm, "end": v(29.5, -26.23) * mm});
            skLineSegment(sketch, "E351", {"start": v(29.5, -26.23) * mm, "end": v(28.76, -44.73) * mm});
            skLineSegment(sketch, "E352", {"start": v(28.76, -44.73) * mm, "end": v(28.6, -48.78) * mm});
            skLineSegment(sketch, "E353", {"start": v(28.6, -48.78) * mm, "end": v(28.32, -52.85) * mm});
            skLineSegment(sketch, "E354", {"start": v(28.32, -52.85) * mm, "end": v(27.82, -56.84) * mm});
            skLineSegment(sketch, "E355", {"start": v(27.82, -56.84) * mm, "end": v(27, -60.68) * mm});
            skLineSegment(sketch, "E356", {"start": v(27, -60.68) * mm, "end": v(25.8, -64.28) * mm});
            skLineSegment(sketch, "E357", {"start": v(25.8, -64.28) * mm, "end": v(24.12, -67.56) * mm});
            skLineSegment(sketch, "E358", {"start": v(24.12, -67.56) * mm, "end": v(21.87, -70.44) * mm});
            skLineSegment(sketch, "E359", {"start": v(21.87, -70.44) * mm, "end": v(18.97, -72.84) * mm});
            skLineSegment(sketch, "E360", {"start": v(18.97, -72.84) * mm, "end": v(16.07, -74.29) * mm});
            skLineSegment(sketch, "E361", {"start": v(16.07, -74.29) * mm, "end": v(12.98, -75.03) * mm});
            skLineSegment(sketch, "E362", {"start": v(12.98, -75.03) * mm, "end": v(9.82, -75) * mm});
            skLineSegment(sketch, "E363", {"start": v(9.82, -75) * mm, "end": v(6.73, -74.16) * mm});
            skLineSegment(sketch, "E364", {"start": v(6.73, -74.16) * mm, "end": v(3.8, -72.48) * mm});
            skLineSegment(sketch, "E365", {"start": v(3.8, -72.48) * mm, "end": v(1.44, -70.22) * mm});
            skLineSegment(sketch, "E366", {"start": v(1.44, -70.22) * mm, "end": v(-0.4, -67.48) * mm});
            skLineSegment(sketch, "E367", {"start": v(-0.4, -67.48) * mm, "end": v(-1.8, -64.36) * mm});
            skLineSegment(sketch, "E368", {"start": v(-1.8, -64.36) * mm, "end": v(-2.8, -60.94) * mm});
            skLineSegment(sketch, "E369", {"start": v(-2.8, -60.94) * mm, "end": v(-3.48, -57.31) * mm});
            skLineSegment(sketch, "E370", {"start": v(-3.48, -57.31) * mm, "end": v(-3.91, -53.58) * mm});
            skLineSegment(sketch, "E371", {"start": v(-3.91, -53.58) * mm, "end": v(-4.15, -49.84) * mm});
            skLineSegment(sketch, "E372", {"start": v(-4.15, -49.84) * mm, "end": v(-4.73, -33.17) * mm});
            skLineSegment(sketch, "E373", {"start": v(-4.73, -33.17) * mm, "end": v(-4.86, -16.28) * mm});
            skLineSegment(sketch, "E374", {"start": v(-4.86, -16.28) * mm, "end": v(-4.24, 0.64) * mm});
            skLineSegment(sketch, "E375", {"start": v(-4.24, 0.64) * mm, "end": v(-2.6, 17.43) * mm});
            skLineSegment(sketch, "E376", {"start": v(-2.6, 17.43) * mm, "end": v(-2.28, 19.92) * mm});
            skLineSegment(sketch, "E377", {"start": v(-2.28, 19.92) * mm, "end": v(-2.2, 22.38) * mm});
            skLineSegment(sketch, "E378", {"start": v(-2.2, 22.38) * mm, "end": v(-2.65, 24.68) * mm});
            skLineSegment(sketch, "E379", {"start": v(-2.65, 24.68) * mm, "end": v(-3.91, 26.67) * mm});
            skLineSegment(sketch, "E380", {"start": v(-3.91, 26.67) * mm, "end": v(-5.93, 28) * mm});
            skLineSegment(sketch, "E381", {"start": v(-5.93, 28) * mm, "end": v(-8.25, 28.44) * mm});
            skLineSegment(sketch, "E382", {"start": v(-8.25, 28.44) * mm, "end": v(-10.58, 28) * mm});
            skLineSegment(sketch, "E383", {"start": v(-10.58, 28) * mm, "end": v(-12.6, 26.67) * mm});
            skLineSegment(sketch, "E384", {"start": v(-12.6, 26.67) * mm, "end": v(-13.87, 24.83) * mm});
            skLineSegment(sketch, "E385", {"start": v(-13.87, 24.83) * mm, "end": v(-14.4, 22.7) * mm});
            skLineSegment(sketch, "E386", {"start": v(-14.4, 22.7) * mm, "end": v(-14.43, 20.41) * mm});
            skLineSegment(sketch, "E387", {"start": v(-14.43, 20.41) * mm, "end": v(-14.2, 18.09) * mm});
            skLineSegment(sketch, "E388", {"start": v(-14.2, 18.09) * mm, "end": v(-11.12, -10.33) * mm});
            skLineSegment(sketch, "E389", {"start": v(-11.12, -10.33) * mm, "end": v(-9.87, -38.77) * mm});
            skLineSegment(sketch, "E390", {"start": v(-9.87, -38.77) * mm, "end": v(-10.37, -57.7) * mm});
            skLineSegment(sketch, "E391", {"start": v(-10.37, -57.7) * mm, "end": v(-10.78, -76.62) * mm});
            skLineSegment(sketch, "E392", {"start": v(-10.78, -76.62) * mm, "end": v(-11.11, -79.86) * mm});
            skLineSegment(sketch, "E393", {"start": v(-11.11, -79.86) * mm, "end": v(-12.16, -82.62) * mm});
            skLineSegment(sketch, "E394", {"start": v(-12.16, -82.62) * mm, "end": v(-13.91, -84.44) * mm});
            skLineSegment(sketch, "E395", {"start": v(-13.91, -84.44) * mm, "end": v(-16.35, -84.87) * mm});
            skLineSegment(sketch, "E396", {"start": v(-16.35, -84.87) * mm, "end": v(-18.04, -84.14) * mm});
            skLineSegment(sketch, "E397", {"start": v(-18.04, -84.14) * mm, "end": v(-19.2, -82.73) * mm});
            skLineSegment(sketch, "E398", {"start": v(-19.2, -82.73) * mm, "end": v(-19.9, -80.88) * mm});
            skLineSegment(sketch, "E399", {"start": v(-19.9, -80.88) * mm, "end": v(-20.27, -78.86) * mm});
            skLineSegment(sketch, "E400", {"start": v(-20.27, -78.86) * mm, "end": v(-21.16, -67.73) * mm});
            skLineSegment(sketch, "E401", {"start": v(-21.16, -67.73) * mm, "end": v(-21.16, -56.6) * mm});
            skLineSegment(sketch, "E402", {"start": v(-21.16, -56.6) * mm, "end": v(-20.1, -45.54) * mm});
            skLineSegment(sketch, "E403", {"start": v(-20.1, -45.54) * mm, "end": v(-17.82, -34.62) * mm});
            skLineSegment(sketch, "E404", {"start": v(-17.82, -34.62) * mm, "end": v(-17.17, -32.12) * mm});
            skLineSegment(sketch, "E405", {"start": v(-17.17, -32.12) * mm, "end": v(-16.76, -29.6) * mm});
            skLineSegment(sketch, "E406", {"start": v(-16.76, -29.6) * mm, "end": v(-16.86, -27.17) * mm});
            skLineSegment(sketch, "E407", {"start": v(-16.86, -27.17) * mm, "end": v(-17.77, -24.87) * mm});
            skLineSegment(sketch, "E408", {"start": v(-17.77, -24.87) * mm, "end": v(-19.17, -23.27) * mm});
            skLineSegment(sketch, "E409", {"start": v(-19.17, -23.27) * mm, "end": v(-20.88, -22.14) * mm});
            skLineSegment(sketch, "E410", {"start": v(-20.88, -22.14) * mm, "end": v(-22.8, -21.5) * mm});
            skLineSegment(sketch, "E411", {"start": v(-22.8, -21.5) * mm, "end": v(-24.82, -21.32) * mm});
            skLineSegment(sketch, "E412", {"start": v(-24.82, -21.32) * mm, "end": v(-26.82, -21.62) * mm});
            skLineSegment(sketch, "E413", {"start": v(-26.82, -21.62) * mm, "end": v(-28.67, -22.38) * mm});
            skLineSegment(sketch, "E414", {"start": v(-28.67, -22.38) * mm, "end": v(-30.26, -23.6) * mm});
            skLineSegment(sketch, "E415", {"start": v(-30.26, -23.6) * mm, "end": v(-31.48, -25.28) * mm});
            skLineSegment(sketch, "E416", {"start": v(-31.48, -25.28) * mm, "end": v(-32.14, -27.62) * mm});
            skLineSegment(sketch, "E417", {"start": v(-32.14, -27.62) * mm, "end": v(-31.96, -30.04) * mm});
            skLineSegment(sketch, "E418", {"start": v(-31.96, -30.04) * mm, "end": v(-31.28, -32.48) * mm});
            skLineSegment(sketch, "E419", {"start": v(-31.28, -32.48) * mm, "end": v(-30.42, -34.92) * mm});
            skLineSegment(sketch, "E420", {"start": v(-30.42, -34.92) * mm, "end": v(-28.5, -42.28) * mm});
            skLineSegment(sketch, "E421", {"start": v(-28.5, -42.28) * mm, "end": v(-27.57, -49.81) * mm});
            skLineSegment(sketch, "E422", {"start": v(-27.57, -49.81) * mm, "end": v(-27.28, -57.45) * mm});
            skLineSegment(sketch, "E423", {"start": v(-27.28, -57.45) * mm, "end": v(-27.32, -65.11) * mm});
            skLineSegment(sketch, "E424", {"start": v(-27.32, -65.11) * mm, "end": v(-27.5, -67.36) * mm});
            skLineSegment(sketch, "E425", {"start": v(-27.5, -67.36) * mm, "end": v(-27.93, -69.48) * mm});
            skLineSegment(sketch, "E426", {"start": v(-27.93, -69.48) * mm, "end": v(-28.6, -71.4) * mm});
            skLineSegment(sketch, "E427", {"start": v(-28.6, -71.4) * mm, "end": v(-29.51, -73.05) * mm});
            skLineSegment(sketch, "E428", {"start": v(-29.51, -73.05) * mm, "end": v(-30.62, -74.35) * mm});
            skLineSegment(sketch, "E429", {"start": v(-30.62, -74.35) * mm, "end": v(-31.92, -75.2) * mm});
            skLineSegment(sketch, "E430", {"start": v(-31.92, -75.2) * mm, "end": v(-33.4, -75.57) * mm});
            skLineSegment(sketch, "E431", {"start": v(-33.4, -75.57) * mm, "end": v(-35.01, -75.34) * mm});
            skLineSegment(sketch, "E432", {"start": v(-35.01, -75.34) * mm, "end": v(-36.32, -74.65) * mm});
            skLineSegment(sketch, "E433", {"start": v(-36.32, -74.65) * mm, "end": v(-37.3, -73.61) * mm});
            skLineSegment(sketch, "E434", {"start": v(-37.3, -73.61) * mm, "end": v(-38.02, -72.34) * mm});
            skLineSegment(sketch, "E435", {"start": v(-38.02, -72.34) * mm, "end": v(-38.55, -70.94) * mm});
            skLineSegment(sketch, "E436", {"start": v(-38.55, -70.94) * mm, "end": v(-39.73, -66.65) * mm});
            skLineSegment(sketch, "E437", {"start": v(-39.73, -66.65) * mm, "end": v(-40.48, -62.17) * mm});
            skLineSegment(sketch, "E438", {"start": v(-40.48, -62.17) * mm, "end": v(-40.6, -57.62) * mm});
            skLineSegment(sketch, "E439", {"start": v(-40.6, -57.62) * mm, "end": v(-39.84, -53.1) * mm});
            skLineSegment(sketch, "E440", {"start": v(-39.84, -53.1) * mm, "end": v(-38.93, -49.88) * mm});
            skLineSegment(sketch, "E441", {"start": v(-38.93, -49.88) * mm, "end": v(-38.3, -46.7) * mm});
            skLineSegment(sketch, "E442", {"start": v(-38.3, -46.7) * mm, "end": v(-38.47, -43.69) * mm});
            skLineSegment(sketch, "E443", {"start": v(-38.47, -43.69) * mm, "end": v(-39.93, -41) * mm});
            skLineSegment(sketch, "E444", {"start": v(-39.93, -41) * mm, "end": v(-41.97, -39.53) * mm});
            skLineSegment(sketch, "E445", {"start": v(-41.97, -39.53) * mm, "end": v(-44.38, -38.9) * mm});
            skLineSegment(sketch, "E446", {"start": v(-44.38, -38.9) * mm, "end": v(-46.86, -39.13) * mm});
            skLineSegment(sketch, "E447", {"start": v(-46.86, -39.13) * mm, "end": v(-49.09, -40.28) * mm});
            skLineSegment(sketch, "E448", {"start": v(-49.09, -40.28) * mm, "end": v(-51, -43.02) * mm});
            skLineSegment(sketch, "E449", {"start": v(-51, -43.02) * mm, "end": v(-51.2, -46.31) * mm});
            skLineSegment(sketch, "E450", {"start": v(-51.2, -46.31) * mm, "end": v(-50.31, -49.87) * mm});
            skLineSegment(sketch, "E451", {"start": v(-50.31, -49.87) * mm, "end": v(-48.9, -53.44) * mm});
            skLineSegment(sketch, "E452", {"start": v(-48.9, -53.44) * mm, "end": v(-47.4, -58.84) * mm});
            skLineSegment(sketch, "E453", {"start": v(-47.4, -58.84) * mm, "end": v(-46.95, -64.43) * mm});
            skLineSegment(sketch, "E454", {"start": v(-46.95, -64.43) * mm, "end": v(-47.07, -70.01) * mm});
            skLineSegment(sketch, "E455", {"start": v(-47.07, -70.01) * mm, "end": v(-47.25, -75.37) * mm});
            skLineSegment(sketch, "E456", {"start": v(-47.25, -75.37) * mm, "end": v(-47.56, -78.7) * mm});
            skLineSegment(sketch, "E457", {"start": v(-47.56, -78.7) * mm, "end": v(-48.52, -81.38) * mm});
            skLineSegment(sketch, "E458", {"start": v(-48.52, -81.38) * mm, "end": v(-50.27, -83) * mm});
            skLineSegment(sketch, "E459", {"start": v(-50.27, -83) * mm, "end": v(-52.93, -83.17) * mm});
            skLineSegment(sketch, "E460", {"start": v(-52.93, -83.17) * mm, "end": v(-54.68, -82.3) * mm});
            skLineSegment(sketch, "E461", {"start": v(-54.68, -82.3) * mm, "end": v(-55.79, -80.78) * mm});
            skLineSegment(sketch, "E462", {"start": v(-55.79, -80.78) * mm, "end": v(-56.39, -78.84) * mm});
            skLineSegment(sketch, "E463", {"start": v(-56.39, -78.84) * mm, "end": v(-56.62, -76.72) * mm});
            skLineSegment(sketch, "E464", {"start": v(-56.62, -76.72) * mm, "end": v(-57.06, -68.9) * mm});
            skLineSegment(sketch, "E465", {"start": v(-57.06, -68.9) * mm, "end": v(-57.58, -61.05) * mm});
            skLineSegment(sketch, "E466", {"start": v(-57.58, -61.05) * mm, "end": v(-58.04, -53.2) * mm});
            skLineSegment(sketch, "E467", {"start": v(-58.04, -53.2) * mm, "end": v(-58.32, -45.36) * mm});
            skLineSegment(sketch, "E468", {"start": v(-58.32, -45.36) * mm, "end": v(-58.27, -37.55) * mm});
            skLineSegment(sketch, "E469", {"start": v(-58.27, -37.55) * mm, "end": v(-57.76, -29.79) * mm});
            skLineSegment(sketch, "E470", {"start": v(-57.76, -29.79) * mm, "end": v(-56.65, -22.08) * mm});
            skLineSegment(sketch, "E471", {"start": v(-56.65, -22.08) * mm, "end": v(-54.82, -14.45) * mm});
            skLineSegment(sketch, "E472", {"start": v(-54.82, -14.45) * mm, "end": v(-53.92, -11.3) * mm});
            skLineSegment(sketch, "E473", {"start": v(-53.92, -11.3) * mm, "end": v(-53.35, -8.14) * mm});
            skLineSegment(sketch, "E474", {"start": v(-53.35, -8.14) * mm, "end": v(-53.49, -5.08) * mm});
            skLineSegment(sketch, "E475", {"start": v(-53.49, -5.08) * mm, "end": v(-54.73, -2.25) * mm});
            skLineSegment(sketch, "E476", {"start": v(-54.73, -2.25) * mm, "end": v(-57.85, 0.35) * mm});
            skLineSegment(sketch, "E477", {"start": v(-57.85, 0.35) * mm, "end": v(-61.71, 1.22) * mm});
            skLineSegment(sketch, "E478", {"start": v(-61.71, 1.22) * mm, "end": v(-65.55, 0.36) * mm});
            skLineSegment(sketch, "E479", {"start": v(-65.55, 0.36) * mm, "end": v(-68.56, -2.25) * mm});
            skLineSegment(sketch, "E480", {"start": v(-68.56, -2.25) * mm, "end": v(-69.63, -4.95) * mm});
            skLineSegment(sketch, "E481", {"start": v(-69.63, -4.95) * mm, "end": v(-69.62, -7.84) * mm});
            skLineSegment(sketch, "E482", {"start": v(-69.62, -7.84) * mm, "end": v(-68.98, -10.84) * mm});
            skLineSegment(sketch, "E483", {"start": v(-68.98, -10.84) * mm, "end": v(-68.12, -13.83) * mm});
            skLineSegment(sketch, "E484", {"start": v(-68.12, -13.83) * mm, "end": v(-65.73, -26.37) * mm});
            skLineSegment(sketch, "E485", {"start": v(-65.73, -26.37) * mm, "end": v(-65.08, -39.12) * mm});
            skLineSegment(sketch, "E486", {"start": v(-65.08, -39.12) * mm, "end": v(-65.6, -51.97) * mm});
            skLineSegment(sketch, "E487", {"start": v(-65.6, -51.97) * mm, "end": v(-66.75, -64.81) * mm});
            skLineSegment(sketch, "E488", {"start": v(-66.75, -64.81) * mm, "end": v(-67.4, -68.26) * mm});
            skLineSegment(sketch, "E489", {"start": v(-67.4, -68.26) * mm, "end": v(-68.56, -71.2) * mm});
            skLineSegment(sketch, "E490", {"start": v(-68.56, -71.2) * mm, "end": v(-70.1, -73.59) * mm});
            skLineSegment(sketch, "E491", {"start": v(-70.1, -73.59) * mm, "end": v(-71.88, -75.35) * mm});
            skLineSegment(sketch, "E492", {"start": v(-71.88, -75.35) * mm, "end": v(-73.79, -76.45) * mm});
            skLineSegment(sketch, "E493", {"start": v(-73.79, -76.45) * mm, "end": v(-75.7, -76.81) * mm});
            skLineSegment(sketch, "E494", {"start": v(-75.7, -76.81) * mm, "end": v(-77.5, -76.38) * mm});
            skLineSegment(sketch, "E495", {"start": v(-77.5, -76.38) * mm, "end": v(-79.03, -75.11) * mm});
            skLineSegment(sketch, "E496", {"start": v(-79.03, -75.11) * mm, "end": v(-79.96, -72.83) * mm});
            skLineSegment(sketch, "E497", {"start": v(-79.96, -72.83) * mm, "end": v(-80.1, -70.24) * mm});
            skLineSegment(sketch, "E498", {"start": v(-80.1, -70.24) * mm, "end": v(-80.32, -67.7) * mm});
            skLineSegment(sketch, "E499", {"start": v(-80.32, -67.7) * mm, "end": v(-81.48, -65.56) * mm});
            skLineSegment(sketch, "E500", {"start": v(-81.48, -65.56) * mm, "end": v(-82.75, -64.77) * mm});
            skLineSegment(sketch, "E501", {"start": v(-82.75, -64.77) * mm, "end": v(-84.19, -64.56) * mm});
            skLineSegment(sketch, "E502", {"start": v(-84.19, -64.56) * mm, "end": v(-85.64, -64.91) * mm});
            skLineSegment(sketch, "E503", {"start": v(-85.64, -64.91) * mm, "end": v(-86.99, -65.77) * mm});
            skLineSegment(sketch, "E504", {"start": v(-86.99, -65.77) * mm, "end": v(-88.32, -67.44) * mm});
            skLineSegment(sketch, "E505", {"start": v(-88.32, -67.44) * mm, "end": v(-89, -69.33) * mm});
            skLineSegment(sketch, "E506", {"start": v(-89, -69.33) * mm, "end": v(-89.17, -71.39) * mm});
            skLineSegment(sketch, "E507", {"start": v(-89.17, -71.39) * mm, "end": v(-89.05, -73.56) * mm});
            skLineSegment(sketch, "E508", {"start": v(-89.05, -73.56) * mm, "end": v(-88.78, -75.8) * mm});
            skLineSegment(sketch, "E509", {"start": v(-88.78, -75.8) * mm, "end": v(-88.56, -78.05) * mm});
            skLineSegment(sketch, "E510", {"start": v(-88.56, -78.05) * mm, "end": v(-88.55, -80.26) * mm});
            skLineSegment(sketch, "E511", {"start": v(-88.55, -80.26) * mm, "end": v(-88.94, -82.37) * mm});
            skLineSegment(sketch, "E512", {"start": v(-88.94, -82.37) * mm, "end": v(-89.7, -84.12) * mm});
            skLineSegment(sketch, "E513", {"start": v(-89.7, -84.12) * mm, "end": v(-90.7, -85.73) * mm});
            skLineSegment(sketch, "E514", {"start": v(-90.7, -85.73) * mm, "end": v(-91.78, -87.3) * mm});
            skLineSegment(sketch, "E515", {"start": v(-91.78, -87.3) * mm, "end": v(-92.76, -88.92) * mm});
            skLineSegment(sketch, "E516", {"start": v(-92.76, -88.92) * mm, "end": v(-93.75, -91.52) * mm});
            skLineSegment(sketch, "E517", {"start": v(-93.75, -91.52) * mm, "end": v(-94.12, -94.31) * mm});
            skLineSegment(sketch, "E518", {"start": v(-94.12, -94.31) * mm, "end": v(90.97, -94.31) * mm});
            skSolve(sketch);
        }
        {
            var Q0;
            Q0=qSketchRegion(id+"F0",true);
            extrude(context, id + "F1", {"entities" : qUnion([Q0]), "depth" : .8 * mm});
        }
        {
            var Q0;
            Q0=makeQuery(id+"F1.opExtrude","CAP_FACE",FACE,{"disambiguationData":[OSD([sQuery(id+"F0.wireOp",EDGE,"E1"),sQuery(id+"F0.wireOp",EDGE,"E2"),sQuery(id+"F0.wireOp",EDGE,"E3"),sQuery(id+"F0.wireOp",EDGE,"E4"),sQuery(id+"F0.wireOp",EDGE,"E5"),sQuery(id+"F0.wireOp",EDGE,"E6"),sQuery(id+"F0.wireOp",EDGE,"E7"),sQuery(id+"F0.wireOp",EDGE,"E8"),sQuery(id+"F0.wireOp",EDGE,"E9"),sQuery(id+"F0.wireOp",EDGE,"E10"),sQuery(id+"F0.wireOp",EDGE,"E11"),sQuery(id+"F0.wireOp",EDGE,"E12"),sQuery(id+"F0.wireOp",EDGE,"E13"),sQuery(id+"F0.wireOp",EDGE,"E14"),sQuery(id+"F0.wireOp",EDGE,"E15"),sQuery(id+"F0.wireOp",EDGE,"E16"),sQuery(id+"F0.wireOp",EDGE,"E17"),sQuery(id+"F0.wireOp",EDGE,"E18"),sQuery(id+"F0.wireOp",EDGE,"E19"),sQuery(id+"F0.wireOp",EDGE,"E20"),sQuery(id+"F0.wireOp",EDGE,"E21"),sQuery(id+"F0.wireOp",EDGE,"E22"),sQuery(id+"F0.wireOp",EDGE,"E23"),sQuery(id+"F0.wireOp",EDGE,"E24"),sQuery(id+"F0.wireOp",EDGE,"E25"),sQuery(id+"F0.wireOp",EDGE,"E26"),sQuery(id+"F0.wireOp",EDGE,"E27"),sQuery(id+"F0.wireOp",EDGE,"E28"),sQuery(id+"F0.wireOp",EDGE,"E29"),sQuery(id+"F0.wireOp",EDGE,"E30"),sQuery(id+"F0.wireOp",EDGE,"E31"),sQuery(id+"F0.wireOp",EDGE,"E32"),sQuery(id+"F0.wireOp",EDGE,"E33"),sQuery(id+"F0.wireOp",EDGE,"E34"),sQuery(id+"F0.wireOp",EDGE,"E35"),sQuery(id+"F0.wireOp",EDGE,"E36"),sQuery(id+"F0.wireOp",EDGE,"E37"),sQuery(id+"F0.wireOp",EDGE,"E38"),sQuery(id+"F0.wireOp",EDGE,"E39"),sQuery(id+"F0.wireOp",EDGE,"E40"),sQuery(id+"F0.wireOp",EDGE,"E41"),sQuery(id+"F0.wireOp",EDGE,"E42"),sQuery(id+"F0.wireOp",EDGE,"E43"),sQuery(id+"F0.wireOp",EDGE,"E44"),sQuery(id+"F0.wireOp",EDGE,"E45"),sQuery(id+"F0.wireOp",EDGE,"E46"),sQuery(id+"F0.wireOp",EDGE,"E47"),sQuery(id+"F0.wireOp",EDGE,"E48"),sQuery(id+"F0.wireOp",EDGE,"E49"),sQuery(id+"F0.wireOp",EDGE,"E50"),sQuery(id+"F0.wireOp",EDGE,"E51"),sQuery(id+"F0.wireOp",EDGE,"E52"),sQuery(id+"F0.wireOp",EDGE,"E53"),sQuery(id+"F0.wireOp",EDGE,"E54"),sQuery(id+"F0.wireOp",EDGE,"E55"),sQuery(id+"F0.wireOp",EDGE,"E56"),sQuery(id+"F0.wireOp",EDGE,"E57"),sQuery(id+"F0.wireOp",EDGE,"E58"),sQuery(id+"F0.wireOp",EDGE,"E59"),sQuery(id+"F0.wireOp",EDGE,"E60"),sQuery(id+"F0.wireOp",EDGE,"E61"),sQuery(id+"F0.wireOp",EDGE,"E62"),sQuery(id+"F0.wireOp",EDGE,"E63"),sQuery(id+"F0.wireOp",EDGE,"E64"),sQuery(id+"F0.wireOp",EDGE,"E65"),sQuery(id+"F0.wireOp",EDGE,"E66"),sQuery(id+"F0.wireOp",EDGE,"E67"),sQuery(id+"F0.wireOp",EDGE,"E68"),sQuery(id+"F0.wireOp",EDGE,"E69"),sQuery(id+"F0.wireOp",EDGE,"E70"),sQuery(id+"F0.wireOp",EDGE,"E71"),sQuery(id+"F0.wireOp",EDGE,"E72"),sQuery(id+"F0.wireOp",EDGE,"E73"),sQuery(id+"F0.wireOp",EDGE,"E74"),sQuery(id+"F0.wireOp",EDGE,"E75"),sQuery(id+"F0.wireOp",EDGE,"E76"),sQuery(id+"F0.wireOp",EDGE,"E77"),sQuery(id+"F0.wireOp",EDGE,"E78"),sQuery(id+"F0.wireOp",EDGE,"E79"),sQuery(id+"F0.wireOp",EDGE,"E80"),sQuery(id+"F0.wireOp",EDGE,"E81"),sQuery(id+"F0.wireOp",EDGE,"E82"),sQuery(id+"F0.wireOp",EDGE,"E83"),sQuery(id+"F0.wireOp",EDGE,"E84"),sQuery(id+"F0.wireOp",EDGE,"E85"),sQuery(id+"F0.wireOp",EDGE,"E86"),sQuery(id+"F0.wireOp",EDGE,"E87"),sQuery(id+"F0.wireOp",EDGE,"E88"),sQuery(id+"F0.wireOp",EDGE,"E89"),sQuery(id+"F0.wireOp",EDGE,"E90"),sQuery(id+"F0.wireOp",EDGE,"E91"),sQuery(id+"F0.wireOp",EDGE,"E92"),sQuery(id+"F0.wireOp",EDGE,"E93"),sQuery(id+"F0.wireOp",EDGE,"E94"),sQuery(id+"F0.wireOp",EDGE,"E95"),sQuery(id+"F0.wireOp",EDGE,"E96"),sQuery(id+"F0.wireOp",EDGE,"E97"),sQuery(id+"F0.wireOp",EDGE,"E98"),sQuery(id+"F0.wireOp",EDGE,"E99"),sQuery(id+"F0.wireOp",EDGE,"E100"),sQuery(id+"F0.wireOp",EDGE,"E101"),sQuery(id+"F0.wireOp",EDGE,"E102"),sQuery(id+"F0.wireOp",EDGE,"E103"),sQuery(id+"F0.wireOp",EDGE,"E104"),sQuery(id+"F0.wireOp",EDGE,"E105"),sQuery(id+"F0.wireOp",EDGE,"E106"),sQuery(id+"F0.wireOp",EDGE,"E107"),sQuery(id+"F0.wireOp",EDGE,"E108"),sQuery(id+"F0.wireOp",EDGE,"E109"),sQuery(id+"F0.wireOp",EDGE,"E110"),sQuery(id+"F0.wireOp",EDGE,"E111"),sQuery(id+"F0.wireOp",EDGE,"E112"),sQuery(id+"F0.wireOp",EDGE,"E113"),sQuery(id+"F0.wireOp",EDGE,"E114"),sQuery(id+"F0.wireOp",EDGE,"E115"),sQuery(id+"F0.wireOp",EDGE,"E116"),sQuery(id+"F0.wireOp",EDGE,"E117"),sQuery(id+"F0.wireOp",EDGE,"E118"),sQuery(id+"F0.wireOp",EDGE,"E119"),sQuery(id+"F0.wireOp",EDGE,"E120"),sQuery(id+"F0.wireOp",EDGE,"E121"),sQuery(id+"F0.wireOp",EDGE,"E122"),sQuery(id+"F0.wireOp",EDGE,"E123"),sQuery(id+"F0.wireOp",EDGE,"E124"),sQuery(id+"F0.wireOp",EDGE,"E125"),sQuery(id+"F0.wireOp",EDGE,"E126"),sQuery(id+"F0.wireOp",EDGE,"E127"),sQuery(id+"F0.wireOp",EDGE,"E128"),sQuery(id+"F0.wireOp",EDGE,"E129"),sQuery(id+"F0.wireOp",EDGE,"E130"),sQuery(id+"F0.wireOp",EDGE,"E131"),sQuery(id+"F0.wireOp",EDGE,"E132"),sQuery(id+"F0.wireOp",EDGE,"E133"),sQuery(id+"F0.wireOp",EDGE,"E134"),sQuery(id+"F0.wireOp",EDGE,"E135"),sQuery(id+"F0.wireOp",EDGE,"E136"),sQuery(id+"F0.wireOp",EDGE,"E137"),sQuery(id+"F0.wireOp",EDGE,"E138"),sQuery(id+"F0.wireOp",EDGE,"E139"),sQuery(id+"F0.wireOp",EDGE,"E140"),sQuery(id+"F0.wireOp",EDGE,"E141"),sQuery(id+"F0.wireOp",EDGE,"E142"),sQuery(id+"F0.wireOp",EDGE,"E143"),sQuery(id+"F0.wireOp",EDGE,"E144"),sQuery(id+"F0.wireOp",EDGE,"E145"),sQuery(id+"F0.wireOp",EDGE,"E146"),sQuery(id+"F0.wireOp",EDGE,"E147"),sQuery(id+"F0.wireOp",EDGE,"E148"),sQuery(id+"F0.wireOp",EDGE,"E149"),sQuery(id+"F0.wireOp",EDGE,"E150"),sQuery(id+"F0.wireOp",EDGE,"E151"),sQuery(id+"F0.wireOp",EDGE,"E152"),sQuery(id+"F0.wireOp",EDGE,"E153"),sQuery(id+"F0.wireOp",EDGE,"E154"),sQuery(id+"F0.wireOp",EDGE,"E155"),sQuery(id+"F0.wireOp",EDGE,"E156"),sQuery(id+"F0.wireOp",EDGE,"E157"),sQuery(id+"F0.wireOp",EDGE,"E158"),sQuery(id+"F0.wireOp",EDGE,"E159"),sQuery(id+"F0.wireOp",EDGE,"E160"),sQuery(id+"F0.wireOp",EDGE,"E161"),sQuery(id+"F0.wireOp",EDGE,"E162"),sQuery(id+"F0.wireOp",EDGE,"E163"),sQuery(id+"F0.wireOp",EDGE,"E164"),sQuery(id+"F0.wireOp",EDGE,"E165"),sQuery(id+"F0.wireOp",EDGE,"E166"),sQuery(id+"F0.wireOp",EDGE,"E167"),sQuery(id+"F0.wireOp",EDGE,"E168"),sQuery(id+"F0.wireOp",EDGE,"E169"),sQuery(id+"F0.wireOp",EDGE,"E170"),sQuery(id+"F0.wireOp",EDGE,"E171"),sQuery(id+"F0.wireOp",EDGE,"E172"),sQuery(id+"F0.wireOp",EDGE,"E173"),sQuery(id+"F0.wireOp",EDGE,"E174"),sQuery(id+"F0.wireOp",EDGE,"E175"),sQuery(id+"F0.wireOp",EDGE,"E176"),sQuery(id+"F0.wireOp",EDGE,"E177"),sQuery(id+"F0.wireOp",EDGE,"E178"),sQuery(id+"F0.wireOp",EDGE,"E179"),sQuery(id+"F0.wireOp",EDGE,"E180"),sQuery(id+"F0.wireOp",EDGE,"E181"),sQuery(id+"F0.wireOp",EDGE,"E182"),sQuery(id+"F0.wireOp",EDGE,"E183"),sQuery(id+"F0.wireOp",EDGE,"E184"),sQuery(id+"F0.wireOp",EDGE,"E185"),sQuery(id+"F0.wireOp",EDGE,"E186"),sQuery(id+"F0.wireOp",EDGE,"E187"),sQuery(id+"F0.wireOp",EDGE,"E188"),sQuery(id+"F0.wireOp",EDGE,"E189"),sQuery(id+"F0.wireOp",EDGE,"E190"),sQuery(id+"F0.wireOp",EDGE,"E191"),sQuery(id+"F0.wireOp",EDGE,"E192"),sQuery(id+"F0.wireOp",EDGE,"E193"),sQuery(id+"F0.wireOp",EDGE,"E194"),sQuery(id+"F0.wireOp",EDGE,"E195"),sQuery(id+"F0.wireOp",EDGE,"E196"),sQuery(id+"F0.wireOp",EDGE,"E197"),sQuery(id+"F0.wireOp",EDGE,"E198"),sQuery(id+"F0.wireOp",EDGE,"E199"),sQuery(id+"F0.wireOp",EDGE,"E200"),sQuery(id+"F0.wireOp",EDGE,"E201"),sQuery(id+"F0.wireOp",EDGE,"E202"),sQuery(id+"F0.wireOp",EDGE,"E203"),sQuery(id+"F0.wireOp",EDGE,"E204"),sQuery(id+"F0.wireOp",EDGE,"E205"),sQuery(id+"F0.wireOp",EDGE,"E206"),sQuery(id+"F0.wireOp",EDGE,"E207"),sQuery(id+"F0.wireOp",EDGE,"E208"),sQuery(id+"F0.wireOp",EDGE,"E209"),sQuery(id+"F0.wireOp",EDGE,"E210"),sQuery(id+"F0.wireOp",EDGE,"E211"),sQuery(id+"F0.wireOp",EDGE,"E212"),sQuery(id+"F0.wireOp",EDGE,"E213"),sQuery(id+"F0.wireOp",EDGE,"E214"),sQuery(id+"F0.wireOp",EDGE,"E215"),sQuery(id+"F0.wireOp",EDGE,"E216"),sQuery(id+"F0.wireOp",EDGE,"E217"),sQuery(id+"F0.wireOp",EDGE,"E218"),sQuery(id+"F0.wireOp",EDGE,"E219"),sQuery(id+"F0.wireOp",EDGE,"E220"),sQuery(id+"F0.wireOp",EDGE,"E221"),sQuery(id+"F0.wireOp",EDGE,"E222"),sQuery(id+"F0.wireOp",EDGE,"E223"),sQuery(id+"F0.wireOp",EDGE,"E224"),sQuery(id+"F0.wireOp",EDGE,"E225"),sQuery(id+"F0.wireOp",EDGE,"E226"),sQuery(id+"F0.wireOp",EDGE,"E227"),sQuery(id+"F0.wireOp",EDGE,"E228"),sQuery(id+"F0.wireOp",EDGE,"E229"),sQuery(id+"F0.wireOp",EDGE,"E230"),sQuery(id+"F0.wireOp",EDGE,"E231"),sQuery(id+"F0.wireOp",EDGE,"E232"),sQuery(id+"F0.wireOp",EDGE,"E233"),sQuery(id+"F0.wireOp",EDGE,"E234"),sQuery(id+"F0.wireOp",EDGE,"E235"),sQuery(id+"F0.wireOp",EDGE,"E236"),sQuery(id+"F0.wireOp",EDGE,"E237"),sQuery(id+"F0.wireOp",EDGE,"E238"),sQuery(id+"F0.wireOp",EDGE,"E239"),sQuery(id+"F0.wireOp",EDGE,"E240"),sQuery(id+"F0.wireOp",EDGE,"E241"),sQuery(id+"F0.wireOp",EDGE,"E242"),sQuery(id+"F0.wireOp",EDGE,"E243"),sQuery(id+"F0.wireOp",EDGE,"E244"),sQuery(id+"F0.wireOp",EDGE,"E245"),sQuery(id+"F0.wireOp",EDGE,"E246"),sQuery(id+"F0.wireOp",EDGE,"E247"),sQuery(id+"F0.wireOp",EDGE,"E248"),sQuery(id+"F0.wireOp",EDGE,"E249"),sQuery(id+"F0.wireOp",EDGE,"E250"),sQuery(id+"F0.wireOp",EDGE,"E251"),sQuery(id+"F0.wireOp",EDGE,"E252"),sQuery(id+"F0.wireOp",EDGE,"E253"),sQuery(id+"F0.wireOp",EDGE,"E254"),sQuery(id+"F0.wireOp",EDGE,"E255"),sQuery(id+"F0.wireOp",EDGE,"E256"),sQuery(id+"F0.wireOp",EDGE,"E257"),sQuery(id+"F0.wireOp",EDGE,"E258"),sQuery(id+"F0.wireOp",EDGE,"E259"),sQuery(id+"F0.wireOp",EDGE,"E260"),sQuery(id+"F0.wireOp",EDGE,"E261"),sQuery(id+"F0.wireOp",EDGE,"E262")])],"isStart":false});
            var Q1;
            Q1=makeQuery(id+"F1.opExtrude","CAP_FACE",FACE,{"disambiguationData":[OSD([sQuery(id+"F0.wireOp",EDGE,"E263"),sQuery(id+"F0.wireOp",EDGE,"E264"),sQuery(id+"F0.wireOp",EDGE,"E265"),sQuery(id+"F0.wireOp",EDGE,"E266"),sQuery(id+"F0.wireOp",EDGE,"E267"),sQuery(id+"F0.wireOp",EDGE,"E268"),sQuery(id+"F0.wireOp",EDGE,"E269"),sQuery(id+"F0.wireOp",EDGE,"E270"),sQuery(id+"F0.wireOp",EDGE,"E271"),sQuery(id+"F0.wireOp",EDGE,"E272"),sQuery(id+"F0.wireOp",EDGE,"E273"),sQuery(id+"F0.wireOp",EDGE,"E274"),sQuery(id+"F0.wireOp",EDGE,"E275"),sQuery(id+"F0.wireOp",EDGE,"E276"),sQuery(id+"F0.wireOp",EDGE,"E277"),sQuery(id+"F0.wireOp",EDGE,"E278"),sQuery(id+"F0.wireOp",EDGE,"E279"),sQuery(id+"F0.wireOp",EDGE,"E280"),sQuery(id+"F0.wireOp",EDGE,"E281"),sQuery(id+"F0.wireOp",EDGE,"E282"),sQuery(id+"F0.wireOp",EDGE,"E283"),sQuery(id+"F0.wireOp",EDGE,"E284"),sQuery(id+"F0.wireOp",EDGE,"E285"),sQuery(id+"F0.wireOp",EDGE,"E286"),sQuery(id+"F0.wireOp",EDGE,"E287"),sQuery(id+"F0.wireOp",EDGE,"E288"),sQuery(id+"F0.wireOp",EDGE,"E289"),sQuery(id+"F0.wireOp",EDGE,"E290"),sQuery(id+"F0.wireOp",EDGE,"E291"),sQuery(id+"F0.wireOp",EDGE,"E292"),sQuery(id+"F0.wireOp",EDGE,"E293"),sQuery(id+"F0.wireOp",EDGE,"E294"),sQuery(id+"F0.wireOp",EDGE,"E295"),sQuery(id+"F0.wireOp",EDGE,"E296"),sQuery(id+"F0.wireOp",EDGE,"E297"),sQuery(id+"F0.wireOp",EDGE,"E298"),sQuery(id+"F0.wireOp",EDGE,"E299"),sQuery(id+"F0.wireOp",EDGE,"E300"),sQuery(id+"F0.wireOp",EDGE,"E301"),sQuery(id+"F0.wireOp",EDGE,"E302"),sQuery(id+"F0.wireOp",EDGE,"E303"),sQuery(id+"F0.wireOp",EDGE,"E304"),sQuery(id+"F0.wireOp",EDGE,"E305"),sQuery(id+"F0.wireOp",EDGE,"E306"),sQuery(id+"F0.wireOp",EDGE,"E307"),sQuery(id+"F0.wireOp",EDGE,"E308"),sQuery(id+"F0.wireOp",EDGE,"E309"),sQuery(id+"F0.wireOp",EDGE,"E310"),sQuery(id+"F0.wireOp",EDGE,"E311"),sQuery(id+"F0.wireOp",EDGE,"E312"),sQuery(id+"F0.wireOp",EDGE,"E313"),sQuery(id+"F0.wireOp",EDGE,"E314"),sQuery(id+"F0.wireOp",EDGE,"E315"),sQuery(id+"F0.wireOp",EDGE,"E316"),sQuery(id+"F0.wireOp",EDGE,"E317"),sQuery(id+"F0.wireOp",EDGE,"E318"),sQuery(id+"F0.wireOp",EDGE,"E319"),sQuery(id+"F0.wireOp",EDGE,"E320"),sQuery(id+"F0.wireOp",EDGE,"E321"),sQuery(id+"F0.wireOp",EDGE,"E322"),sQuery(id+"F0.wireOp",EDGE,"E323"),sQuery(id+"F0.wireOp",EDGE,"E324"),sQuery(id+"F0.wireOp",EDGE,"E325"),sQuery(id+"F0.wireOp",EDGE,"E326"),sQuery(id+"F0.wireOp",EDGE,"E327"),sQuery(id+"F0.wireOp",EDGE,"E328"),sQuery(id+"F0.wireOp",EDGE,"E329"),sQuery(id+"F0.wireOp",EDGE,"E330"),sQuery(id+"F0.wireOp",EDGE,"E331"),sQuery(id+"F0.wireOp",EDGE,"E332"),sQuery(id+"F0.wireOp",EDGE,"E333"),sQuery(id+"F0.wireOp",EDGE,"E334"),sQuery(id+"F0.wireOp",EDGE,"E335"),sQuery(id+"F0.wireOp",EDGE,"E336"),sQuery(id+"F0.wireOp",EDGE,"E337"),sQuery(id+"F0.wireOp",EDGE,"E338"),sQuery(id+"F0.wireOp",EDGE,"E339"),sQuery(id+"F0.wireOp",EDGE,"E340"),sQuery(id+"F0.wireOp",EDGE,"E341"),sQuery(id+"F0.wireOp",EDGE,"E342"),sQuery(id+"F0.wireOp",EDGE,"E343"),sQuery(id+"F0.wireOp",EDGE,"E344"),sQuery(id+"F0.wireOp",EDGE,"E345"),sQuery(id+"F0.wireOp",EDGE,"E346"),sQuery(id+"F0.wireOp",EDGE,"E347"),sQuery(id+"F0.wireOp",EDGE,"E348"),sQuery(id+"F0.wireOp",EDGE,"E349"),sQuery(id+"F0.wireOp",EDGE,"E350"),sQuery(id+"F0.wireOp",EDGE,"E351"),sQuery(id+"F0.wireOp",EDGE,"E352"),sQuery(id+"F0.wireOp",EDGE,"E353"),sQuery(id+"F0.wireOp",EDGE,"E354"),sQuery(id+"F0.wireOp",EDGE,"E355"),sQuery(id+"F0.wireOp",EDGE,"E356"),sQuery(id+"F0.wireOp",EDGE,"E357"),sQuery(id+"F0.wireOp",EDGE,"E358"),sQuery(id+"F0.wireOp",EDGE,"E359"),sQuery(id+"F0.wireOp",EDGE,"E360"),sQuery(id+"F0.wireOp",EDGE,"E361"),sQuery(id+"F0.wireOp",EDGE,"E362"),sQuery(id+"F0.wireOp",EDGE,"E363"),sQuery(id+"F0.wireOp",EDGE,"E364"),sQuery(id+"F0.wireOp",EDGE,"E365"),sQuery(id+"F0.wireOp",EDGE,"E366"),sQuery(id+"F0.wireOp",EDGE,"E367"),sQuery(id+"F0.wireOp",EDGE,"E368"),sQuery(id+"F0.wireOp",EDGE,"E369"),sQuery(id+"F0.wireOp",EDGE,"E370"),sQuery(id+"F0.wireOp",EDGE,"E371"),sQuery(id+"F0.wireOp",EDGE,"E372"),sQuery(id+"F0.wireOp",EDGE,"E373"),sQuery(id+"F0.wireOp",EDGE,"E374"),sQuery(id+"F0.wireOp",EDGE,"E375"),sQuery(id+"F0.wireOp",EDGE,"E376"),sQuery(id+"F0.wireOp",EDGE,"E377"),sQuery(id+"F0.wireOp",EDGE,"E378"),sQuery(id+"F0.wireOp",EDGE,"E379"),sQuery(id+"F0.wireOp",EDGE,"E380"),sQuery(id+"F0.wireOp",EDGE,"E381"),sQuery(id+"F0.wireOp",EDGE,"E382"),sQuery(id+"F0.wireOp",EDGE,"E383"),sQuery(id+"F0.wireOp",EDGE,"E384"),sQuery(id+"F0.wireOp",EDGE,"E385"),sQuery(id+"F0.wireOp",EDGE,"E386"),sQuery(id+"F0.wireOp",EDGE,"E387"),sQuery(id+"F0.wireOp",EDGE,"E388"),sQuery(id+"F0.wireOp",EDGE,"E389"),sQuery(id+"F0.wireOp",EDGE,"E390"),sQuery(id+"F0.wireOp",EDGE,"E391"),sQuery(id+"F0.wireOp",EDGE,"E392"),sQuery(id+"F0.wireOp",EDGE,"E393"),sQuery(id+"F0.wireOp",EDGE,"E394"),sQuery(id+"F0.wireOp",EDGE,"E395"),sQuery(id+"F0.wireOp",EDGE,"E396"),sQuery(id+"F0.wireOp",EDGE,"E397"),sQuery(id+"F0.wireOp",EDGE,"E398"),sQuery(id+"F0.wireOp",EDGE,"E399"),sQuery(id+"F0.wireOp",EDGE,"E400"),sQuery(id+"F0.wireOp",EDGE,"E401"),sQuery(id+"F0.wireOp",EDGE,"E402"),sQuery(id+"F0.wireOp",EDGE,"E403"),sQuery(id+"F0.wireOp",EDGE,"E404"),sQuery(id+"F0.wireOp",EDGE,"E405"),sQuery(id+"F0.wireOp",EDGE,"E406"),sQuery(id+"F0.wireOp",EDGE,"E407"),sQuery(id+"F0.wireOp",EDGE,"E408"),sQuery(id+"F0.wireOp",EDGE,"E409"),sQuery(id+"F0.wireOp",EDGE,"E410"),sQuery(id+"F0.wireOp",EDGE,"E411"),sQuery(id+"F0.wireOp",EDGE,"E412"),sQuery(id+"F0.wireOp",EDGE,"E413"),sQuery(id+"F0.wireOp",EDGE,"E414"),sQuery(id+"F0.wireOp",EDGE,"E415"),sQuery(id+"F0.wireOp",EDGE,"E416"),sQuery(id+"F0.wireOp",EDGE,"E417"),sQuery(id+"F0.wireOp",EDGE,"E418"),sQuery(id+"F0.wireOp",EDGE,"E419"),sQuery(id+"F0.wireOp",EDGE,"E420"),sQuery(id+"F0.wireOp",EDGE,"E421"),sQuery(id+"F0.wireOp",EDGE,"E422"),sQuery(id+"F0.wireOp",EDGE,"E423"),sQuery(id+"F0.wireOp",EDGE,"E424"),sQuery(id+"F0.wireOp",EDGE,"E425"),sQuery(id+"F0.wireOp",EDGE,"E426"),sQuery(id+"F0.wireOp",EDGE,"E427"),sQuery(id+"F0.wireOp",EDGE,"E428"),sQuery(id+"F0.wireOp",EDGE,"E429"),sQuery(id+"F0.wireOp",EDGE,"E430"),sQuery(id+"F0.wireOp",EDGE,"E431"),sQuery(id+"F0.wireOp",EDGE,"E432"),sQuery(id+"F0.wireOp",EDGE,"E433"),sQuery(id+"F0.wireOp",EDGE,"E434"),sQuery(id+"F0.wireOp",EDGE,"E435"),sQuery(id+"F0.wireOp",EDGE,"E436"),sQuery(id+"F0.wireOp",EDGE,"E437"),sQuery(id+"F0.wireOp",EDGE,"E438"),sQuery(id+"F0.wireOp",EDGE,"E439"),sQuery(id+"F0.wireOp",EDGE,"E440"),sQuery(id+"F0.wireOp",EDGE,"E441"),sQuery(id+"F0.wireOp",EDGE,"E442"),sQuery(id+"F0.wireOp",EDGE,"E443"),sQuery(id+"F0.wireOp",EDGE,"E444"),sQuery(id+"F0.wireOp",EDGE,"E445"),sQuery(id+"F0.wireOp",EDGE,"E446"),sQuery(id+"F0.wireOp",EDGE,"E447"),sQuery(id+"F0.wireOp",EDGE,"E448"),sQuery(id+"F0.wireOp",EDGE,"E449"),sQuery(id+"F0.wireOp",EDGE,"E450"),sQuery(id+"F0.wireOp",EDGE,"E451"),sQuery(id+"F0.wireOp",EDGE,"E452"),sQuery(id+"F0.wireOp",EDGE,"E453"),sQuery(id+"F0.wireOp",EDGE,"E454"),sQuery(id+"F0.wireOp",EDGE,"E455"),sQuery(id+"F0.wireOp",EDGE,"E456"),sQuery(id+"F0.wireOp",EDGE,"E457"),sQuery(id+"F0.wireOp",EDGE,"E458"),sQuery(id+"F0.wireOp",EDGE,"E459"),sQuery(id+"F0.wireOp",EDGE,"E460"),sQuery(id+"F0.wireOp",EDGE,"E461"),sQuery(id+"F0.wireOp",EDGE,"E462"),sQuery(id+"F0.wireOp",EDGE,"E463"),sQuery(id+"F0.wireOp",EDGE,"E464"),sQuery(id+"F0.wireOp",EDGE,"E465"),sQuery(id+"F0.wireOp",EDGE,"E466"),sQuery(id+"F0.wireOp",EDGE,"E467"),sQuery(id+"F0.wireOp",EDGE,"E468"),sQuery(id+"F0.wireOp",EDGE,"E469"),sQuery(id+"F0.wireOp",EDGE,"E470"),sQuery(id+"F0.wireOp",EDGE,"E471"),sQuery(id+"F0.wireOp",EDGE,"E472"),sQuery(id+"F0.wireOp",EDGE,"E473"),sQuery(id+"F0.wireOp",EDGE,"E474"),sQuery(id+"F0.wireOp",EDGE,"E475"),sQuery(id+"F0.wireOp",EDGE,"E476"),sQuery(id+"F0.wireOp",EDGE,"E477"),sQuery(id+"F0.wireOp",EDGE,"E478"),sQuery(id+"F0.wireOp",EDGE,"E479"),sQuery(id+"F0.wireOp",EDGE,"E480"),sQuery(id+"F0.wireOp",EDGE,"E481"),sQuery(id+"F0.wireOp",EDGE,"E482"),sQuery(id+"F0.wireOp",EDGE,"E483"),sQuery(id+"F0.wireOp",EDGE,"E484"),sQuery(id+"F0.wireOp",EDGE,"E485"),sQuery(id+"F0.wireOp",EDGE,"E486"),sQuery(id+"F0.wireOp",EDGE,"E487"),sQuery(id+"F0.wireOp",EDGE,"E488"),sQuery(id+"F0.wireOp",EDGE,"E489"),sQuery(id+"F0.wireOp",EDGE,"E490"),sQuery(id+"F0.wireOp",EDGE,"E491"),sQuery(id+"F0.wireOp",EDGE,"E492"),sQuery(id+"F0.wireOp",EDGE,"E493"),sQuery(id+"F0.wireOp",EDGE,"E494"),sQuery(id+"F0.wireOp",EDGE,"E495"),sQuery(id+"F0.wireOp",EDGE,"E496"),sQuery(id+"F0.wireOp",EDGE,"E497"),sQuery(id+"F0.wireOp",EDGE,"E498"),sQuery(id+"F0.wireOp",EDGE,"E499"),sQuery(id+"F0.wireOp",EDGE,"E500"),sQuery(id+"F0.wireOp",EDGE,"E501"),sQuery(id+"F0.wireOp",EDGE,"E502"),sQuery(id+"F0.wireOp",EDGE,"E503"),sQuery(id+"F0.wireOp",EDGE,"E504"),sQuery(id+"F0.wireOp",EDGE,"E505"),sQuery(id+"F0.wireOp",EDGE,"E506"),sQuery(id+"F0.wireOp",EDGE,"E507"),sQuery(id+"F0.wireOp",EDGE,"E508"),sQuery(id+"F0.wireOp",EDGE,"E509"),sQuery(id+"F0.wireOp",EDGE,"E510"),sQuery(id+"F0.wireOp",EDGE,"E511"),sQuery(id+"F0.wireOp",EDGE,"E512"),sQuery(id+"F0.wireOp",EDGE,"E513"),sQuery(id+"F0.wireOp",EDGE,"E514"),sQuery(id+"F0.wireOp",EDGE,"E515"),sQuery(id+"F0.wireOp",EDGE,"E516"),sQuery(id+"F0.wireOp",EDGE,"E517"),sQuery(id+"F0.wireOp",EDGE,"E518")])],"isStart":false});
            chamfer(context, id + "F2", {"entities" : qUnion([Q0, Q1]), "chamferType" : ChamferType.OFFSET_ANGLE, "width" : .8 * mm, "oppositeDirection" : true, "angle" : 70 * degree, "tangentPropagation" : true});
        }
    });
